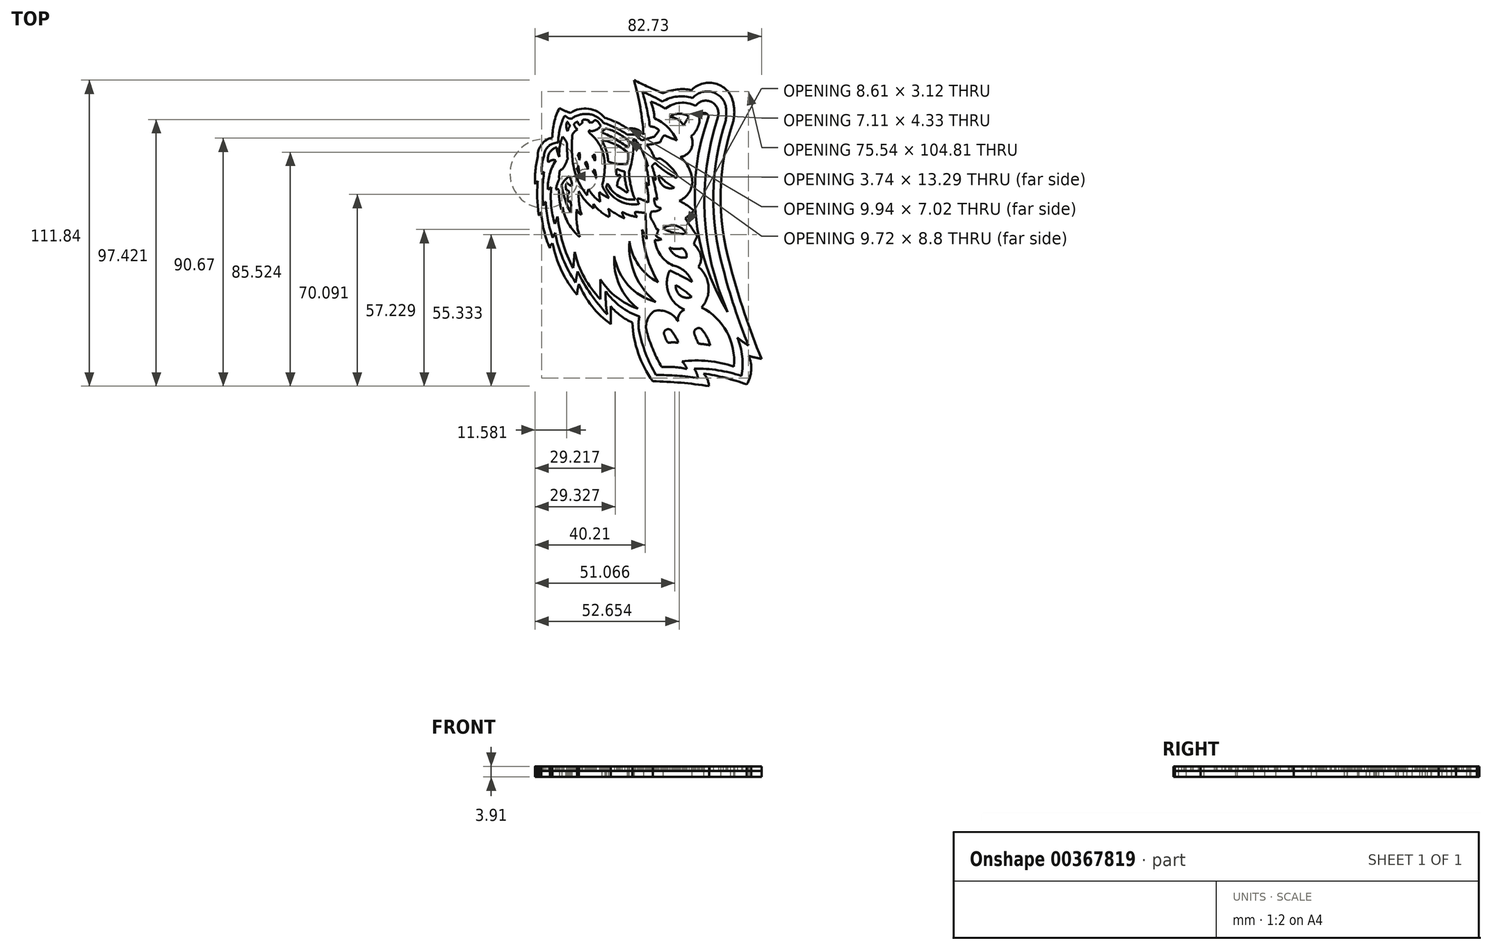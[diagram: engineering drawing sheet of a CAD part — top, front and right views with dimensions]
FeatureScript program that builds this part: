
annotation { "Feature Type Name" : "Feature", "Feature Type Description" : "" }
export const myFeature = defineFeature(function(context is Context, id is Id, definition is map)
    precondition{}
    {
        {
            var Q0;
            Q0=qCreatedBy(makeId("Top.planeOp"),FACE);
            var sketch = newSketch(context, id + "F0", { "sketchPlane" : qUnion([Q0])});
            skLineSegment(sketch, "E0", {"start": v(-9.68, 4.6) * mm, "end": v(-12.98, 4.6) * mm});
            skLineSegment(sketch, "E1", {"start": v(-7.81, 9.13) * mm, "end": v(-5.14, 8.87) * mm});
            skLineSegment(sketch, "E2", {"start": v(-0.46, 12.2) * mm, "end": v(0.77, 11.72) * mm});
            skLineSegment(sketch, "E3", {"start": v(5.28, 13.32) * mm, "end": v(5.62, 12.76) * mm});
            skArc(sketch, "E4", {"start": v(10.1, 12.03) * mm, "mid": v(7.78, 13.04) * mm, "end": v(5.28, 13.32) * mm});
            skArc(sketch, "E5", {"start": v(5.62, 12.76) * mm, "mid": v(2.55, 12.78) * mm, "end": v(-0.46, 12.2) * mm});
            skArc(sketch, "E6", {"start": v(0.77, 11.72) * mm, "mid": v(-3.65, 10.85) * mm, "end": v(-7.81, 9.13) * mm});
            skArc(sketch, "E7", {"start": v(-5.14, 8.87) * mm, "mid": v(-9.36, 7.3) * mm, "end": v(-12.98, 4.6) * mm});
            skArc(sketch, "E8", {"start": v(-9.68, 4.6) * mm, "mid": v(-12.64, 1.92) * mm, "end": v(-14.53, -1.6) * mm});
            skArc(sketch, "E9", {"start": v(-5.85, 2.3) * mm, "mid": v(-10.68, 1.43) * mm, "end": v(-14.53, -1.6) * mm});
            skArc(sketch, "E10", {"start": v(-5.85, 2.3) * mm, "mid": v(-10.66, -0.03) * mm, "end": v(-13.45, -4.58) * mm});
            skArc(sketch, "E11", {"start": v(-3.37, -0.22) * mm, "mid": v(-8.94, -1.17) * mm, "end": v(-13.45, -4.58) * mm});
            skArc(sketch, "E12", {"start": v(-3.37, -0.22) * mm, "mid": v(-7.34, -1.75) * mm, "end": v(-10.14, -4.94) * mm});
            skArc(sketch, "E13", {"start": v(-1.42, -2.32) * mm, "mid": v(-5.93, -3.13) * mm, "end": v(-10.14, -4.94) * mm});
            skArc(sketch, "E14", {"start": v(-1.42, -2.32) * mm, "mid": v(-2.2, -2.67) * mm, "end": v(-2.98, -3.05) * mm});
            skArc(sketch, "E15", {"start": v(-2.98, -3.05) * mm, "mid": v(-0.82, -2.97) * mm, "end": v(1.35, -2.86) * mm});
            skArc(sketch, "E16", {"start": v(1.55, -1.16) * mm, "mid": v(1.44, -2) * mm, "end": v(1.35, -2.86) * mm});
            skArc(sketch, "E17", {"start": v(1.55, -1.16) * mm, "mid": v(1.07, -1.21) * mm, "end": v(0.68, -1.5) * mm});
            skArc(sketch, "E18", {"start": v(1.55, 1.01) * mm, "mid": v(0.98, -0.2) * mm, "end": v(0.68, -1.5) * mm});
            skArc(sketch, "E19", {"start": v(1.55, 1.01) * mm, "mid": v(0.97, 0.86) * mm, "end": v(0.44, 0.6) * mm});
            skArc(sketch, "E20", {"start": v(2.1, 3.35) * mm, "mid": v(1.2, 2.02) * mm, "end": v(0.44, 0.6) * mm});
            skArc(sketch, "E21", {"start": v(0.68, 3.16) * mm, "mid": v(1.4, 3.13) * mm, "end": v(2.1, 3.35) * mm});
            skArc(sketch, "E22", {"start": v(2.8, 5.75) * mm, "mid": v(1.6, 4.58) * mm, "end": v(0.68, 3.16) * mm});
            skArc(sketch, "E23", {"start": v(2.8, 5.75) * mm, "mid": v(2.45, 5.77) * mm, "end": v(2.1, 5.75) * mm});
            skArc(sketch, "E24", {"start": v(4.98, 8.2) * mm, "mid": v(3.41, 7.12) * mm, "end": v(2.1, 5.75) * mm});
            skArc(sketch, "E25", {"start": v(4.98, 8.2) * mm, "mid": v(3, 8.16) * mm, "end": v(1.05, 7.73) * mm});
            skArc(sketch, "E26", {"start": v(1.94, 8.53) * mm, "mid": v(1.4, 8.23) * mm, "end": v(1.05, 7.73) * mm});
            skArc(sketch, "E27", {"start": v(1.94, 8.53) * mm, "mid": v(-0.37, 8.53) * mm, "end": v(-2.64, 8.02) * mm});
            skArc(sketch, "E28", {"start": v(2.29, 10.88) * mm, "mid": v(-0.43, 9.9) * mm, "end": v(-2.64, 8.02) * mm});
            skArc(sketch, "E29", {"start": v(2.29, 10.88) * mm, "mid": v(2.09, 10.98) * mm, "end": v(1.88, 11.07) * mm});
            skArc(sketch, "E30", {"start": v(5.25, 11.51) * mm, "mid": v(3.55, 11.41) * mm, "end": v(1.88, 11.07) * mm});
            skArc(sketch, "E31", {"start": v(5.25, 11.51) * mm, "mid": v(5.3, 11.75) * mm, "end": v(5.25, 11.98) * mm});
            skArc(sketch, "E32", {"start": v(6.95, 11.43) * mm, "mid": v(6.13, 11.8) * mm, "end": v(5.25, 11.98) * mm});
            skArc(sketch, "E33", {"start": v(8.33, 11.35) * mm, "mid": v(7.64, 11.45) * mm, "end": v(6.95, 11.43) * mm});
            skArc(sketch, "E34", {"start": v(8.55, 10.96) * mm, "mid": v(8.5, 11.2) * mm, "end": v(8.33, 11.35) * mm});
            skArc(sketch, "E35", {"start": v(8.55, 10.96) * mm, "mid": v(9.41, 10.45) * mm, "end": v(10.33, 10.05) * mm});
            skArc(sketch, "E36", {"start": v(12.82, 10.15) * mm, "mid": v(11.58, 10.13) * mm, "end": v(10.33, 10.05) * mm});
            skArc(sketch, "E37", {"start": v(12.82, 10.15) * mm, "mid": v(13.46, 10.44) * mm, "end": v(14, 10.88) * mm});
            skArc(sketch, "E38", {"start": v(14, 10.88) * mm, "mid": v(12.37, 11.37) * mm, "end": v(10.67, 11.43) * mm});
            skArc(sketch, "E39", {"start": v(12.27, 11.86) * mm, "mid": v(11.45, 11.74) * mm, "end": v(10.67, 11.43) * mm});
            skArc(sketch, "E40", {"start": v(10.1, 12.03) * mm, "mid": v(10.1, 12.7) * mm, "end": v(9.75, 13.25) * mm});
            skArc(sketch, "E41", {"start": v(12.27, 11.86) * mm, "mid": v(11.3, 13.08) * mm, "end": v(9.75, 13.25) * mm});
            skArc(sketch, "E42", {"start": v(16.51, 10.14) * mm, "mid": v(15.71, 10.28) * mm, "end": v(14.93, 10.05) * mm});
            skArc(sketch, "E43", {"start": v(16.17, 9.93) * mm, "mid": v(16.36, 10) * mm, "end": v(16.51, 10.14) * mm});
            skArc(sketch, "E44", {"start": v(15.52, 9.9) * mm, "mid": v(15.85, 9.7) * mm, "end": v(16.17, 9.93) * mm});
            skArc(sketch, "E45", {"start": v(14.93, 10.05) * mm, "mid": v(15.22, 9.95) * mm, "end": v(15.52, 9.9) * mm});
            skArc(sketch, "E46", {"start": v(6.07, 11.05) * mm, "mid": v(3.67, 10.5) * mm, "end": v(1.42, 9.55) * mm});
            skArc(sketch, "E47", {"start": v(7.46, 9.83) * mm, "mid": v(6.81, 10.5) * mm, "end": v(6.07, 11.05) * mm});
            skArc(sketch, "E48", {"start": v(5.83, 9.35) * mm, "mid": v(6.7, 9.44) * mm, "end": v(7.46, 9.83) * mm});
            skArc(sketch, "E49", {"start": v(6.3, 10.05) * mm, "mid": v(6, 9.74) * mm, "end": v(5.83, 9.35) * mm});
            skArc(sketch, "E50", {"start": v(6.3, 10.05) * mm, "mid": v(6.26, 10.17) * mm, "end": v(6.18, 10.26) * mm});
            skArc(sketch, "E51", {"start": v(6.18, 10.26) * mm, "mid": v(5.66, 10.36) * mm, "end": v(5.14, 10.26) * mm});
            skArc(sketch, "E52", {"start": v(4.58, 9.85) * mm, "mid": v(4.98, 9.89) * mm, "end": v(5.14, 10.26) * mm});
            skArc(sketch, "E53", {"start": v(4.58, 9.85) * mm, "mid": v(4.31, 10.05) * mm, "end": v(3.98, 10.11) * mm});
            skArc(sketch, "E54", {"start": v(3.98, 10.11) * mm, "mid": v(3.54, 10.03) * mm, "end": v(3.14, 9.85) * mm});
            skArc(sketch, "E55", {"start": v(3.35, 9.58) * mm, "mid": v(3.26, 9.72) * mm, "end": v(3.14, 9.85) * mm});
            skArc(sketch, "E56", {"start": v(1.42, 9.55) * mm, "mid": v(2.38, 9.47) * mm, "end": v(3.35, 9.58) * mm});
            skArc(sketch, "E57", {"start": v(10.38, 9.25) * mm, "mid": v(7.14, 8.5) * mm, "end": v(4.28, 6.8) * mm});
            skArc(sketch, "E58", {"start": v(14.46, 9.25) * mm, "mid": v(12.42, 9.35) * mm, "end": v(10.38, 9.25) * mm});
            skArc(sketch, "E59", {"start": v(15.21, 8.4) * mm, "mid": v(14.88, 8.86) * mm, "end": v(14.46, 9.25) * mm});
            skArc(sketch, "E60", {"start": v(16.06, 9.01) * mm, "mid": v(15.59, 8.77) * mm, "end": v(15.21, 8.4) * mm});
            skArc(sketch, "E61", {"start": v(16.54, 8.4) * mm, "mid": v(16.35, 8.74) * mm, "end": v(16.06, 9.01) * mm});
            skArc(sketch, "E62", {"start": v(16.54, 8.4) * mm, "mid": v(16.21, 8.27) * mm, "end": v(15.92, 8.08) * mm});
            skArc(sketch, "E63", {"start": v(16.29, 7.63) * mm, "mid": v(16.12, 7.87) * mm, "end": v(15.92, 8.08) * mm});
            skArc(sketch, "E64", {"start": v(16.8, 7.55) * mm, "mid": v(16.55, 7.62) * mm, "end": v(16.29, 7.63) * mm});
            skArc(sketch, "E65", {"start": v(16.71, 6.51) * mm, "mid": v(16.84, 7.03) * mm, "end": v(16.8, 7.55) * mm});
            skArc(sketch, "E66", {"start": v(16.38, 6.52) * mm, "mid": v(16.55, 6.5) * mm, "end": v(16.71, 6.51) * mm});
            skArc(sketch, "E67", {"start": v(16.38, 6.52) * mm, "mid": v(16.39, 6.2) * mm, "end": v(16.43, 5.9) * mm});
            skArc(sketch, "E68", {"start": v(16.8, 5.4) * mm, "mid": v(16.65, 5.68) * mm, "end": v(16.43, 5.9) * mm});
            skArc(sketch, "E69", {"start": v(15.82, 4.56) * mm, "mid": v(16.37, 4.92) * mm, "end": v(16.8, 5.4) * mm});
            skArc(sketch, "E70", {"start": v(14.95, 6.1) * mm, "mid": v(15.2, 5.23) * mm, "end": v(15.82, 4.56) * mm});
            skArc(sketch, "E71", {"start": v(15.03, 6.33) * mm, "mid": v(14.95, 6.24) * mm, "end": v(14.95, 6.1) * mm});
            skArc(sketch, "E72", {"start": v(15.03, 6.33) * mm, "mid": v(15.02, 6.48) * mm, "end": v(14.88, 6.51) * mm});
            skArc(sketch, "E73", {"start": v(14.88, 6.51) * mm, "mid": v(14.73, 6.48) * mm, "end": v(14.61, 6.38) * mm});
            skArc(sketch, "E74", {"start": v(9.25, 3.89) * mm, "mid": v(12.22, 4.51) * mm, "end": v(14.61, 6.38) * mm});
            skArc(sketch, "E75", {"start": v(5.98, 4.3) * mm, "mid": v(7.6, 3.98) * mm, "end": v(9.25, 3.89) * mm});
            skArc(sketch, "E76", {"start": v(5.98, 4.3) * mm, "mid": v(5.63, 4.2) * mm, "end": v(5.3, 4.04) * mm});
            skArc(sketch, "E77", {"start": v(3.85, 3.19) * mm, "mid": v(4.59, 3.6) * mm, "end": v(5.3, 4.04) * mm});
            skArc(sketch, "E78", {"start": v(4.81, 4.79) * mm, "mid": v(4.27, 4.02) * mm, "end": v(3.85, 3.19) * mm});
            skArc(sketch, "E79", {"start": v(4.81, 4.79) * mm, "mid": v(4, 4.75) * mm, "end": v(3.19, 4.62) * mm});
            skArc(sketch, "E80", {"start": v(5.3, 6.55) * mm, "mid": v(4.13, 5.7) * mm, "end": v(3.19, 4.62) * mm});
            skArc(sketch, "E81", {"start": v(5.3, 6.55) * mm, "mid": v(4.81, 6.76) * mm, "end": v(4.28, 6.8) * mm});
            skArc(sketch, "E82", {"start": v(7.73, 8.16) * mm, "mid": v(8.25, 8.34) * mm, "end": v(8.74, 8.56) * mm});
            skArc(sketch, "E83", {"start": v(8.74, 8.56) * mm, "mid": v(8.94, 8.35) * mm, "end": v(9.23, 8.31) * mm});
            skArc(sketch, "E84", {"start": v(7.73, 8.16) * mm, "mid": v(8.49, 8.18) * mm, "end": v(9.23, 8.31) * mm});
            skArc(sketch, "E85", {"start": v(10.14, 8.12) * mm, "mid": v(10.6, 8.2) * mm, "end": v(11.03, 8.42) * mm});
            skArc(sketch, "E86", {"start": v(11.03, 8.42) * mm, "mid": v(11.18, 8.22) * mm, "end": v(11.42, 8.12) * mm});
            skArc(sketch, "E87", {"start": v(10.14, 8.12) * mm, "mid": v(10.78, 8.02) * mm, "end": v(11.42, 8.12) * mm});
            skArc(sketch, "E88", {"start": v(7.17, 5.33) * mm, "mid": v(7.9, 5.4) * mm, "end": v(8.6, 5.6) * mm});
            skArc(sketch, "E89", {"start": v(8.17, 5.86) * mm, "mid": v(8.38, 5.72) * mm, "end": v(8.6, 5.6) * mm});
            skArc(sketch, "E90", {"start": v(7.17, 5.33) * mm, "mid": v(7.72, 5.51) * mm, "end": v(8.17, 5.86) * mm});
            skArc(sketch, "E91", {"start": v(9.96, 5.53) * mm, "mid": v(10.4, 5.7) * mm, "end": v(10.77, 5.98) * mm});
            skArc(sketch, "E92", {"start": v(10.77, 5.98) * mm, "mid": v(10.9, 5.75) * mm, "end": v(11.15, 5.66) * mm});
            skArc(sketch, "E93", {"start": v(9.96, 5.53) * mm, "mid": v(10.57, 5.48) * mm, "end": v(11.15, 5.66) * mm});
            skArc(sketch, "E94", {"start": v(8.6, 6.68) * mm, "mid": v(9.14, 6.93) * mm, "end": v(9.65, 7.2) * mm});
            skArc(sketch, "E95", {"start": v(9.65, 7.2) * mm, "mid": v(9.74, 7.05) * mm, "end": v(9.88, 6.95) * mm});
            skArc(sketch, "E96", {"start": v(8.6, 6.68) * mm, "mid": v(9.26, 6.73) * mm, "end": v(9.88, 6.95) * mm});
            skArc(sketch, "E97", {"start": v(5.52, 3.63) * mm, "mid": v(3.3, 1.34) * mm, "end": v(2.8, -1.81) * mm});
            skArc(sketch, "E98", {"start": v(3.7, -1.49) * mm, "mid": v(3.25, -1.64) * mm, "end": v(2.8, -1.81) * mm});
            skArc(sketch, "E99", {"start": v(3.64, -2.08) * mm, "mid": v(3.72, -1.79) * mm, "end": v(3.7, -1.49) * mm});
            skArc(sketch, "E100", {"start": v(3.08, -3.32) * mm, "mid": v(3.39, -2.71) * mm, "end": v(3.64, -2.08) * mm});
            skArc(sketch, "E101", {"start": v(3.08, -3.32) * mm, "mid": v(4.74, -3.29) * mm, "end": v(6.35, -2.9) * mm});
            skArc(sketch, "E102", {"start": v(5.9, -3.45) * mm, "mid": v(6.2, -3.23) * mm, "end": v(6.35, -2.9) * mm});
            skArc(sketch, "E103", {"start": v(5.9, -3.45) * mm, "mid": v(7.63, -3.3) * mm, "end": v(9.31, -2.9) * mm});
            skArc(sketch, "E104", {"start": v(9.1, -3.27) * mm, "mid": v(9.24, -3.1) * mm, "end": v(9.31, -2.9) * mm});
            skArc(sketch, "E105", {"start": v(9.1, -3.27) * mm, "mid": v(11.43, -2.43) * mm, "end": v(13.54, -1.16) * mm});
            skArc(sketch, "E106", {"start": v(13.54, -1.16) * mm, "mid": v(13.58, -1) * mm, "end": v(13.54, -0.84) * mm});
            skArc(sketch, "E107", {"start": v(8.15, -0.14) * mm, "mid": v(10.81, -0.75) * mm, "end": v(13.54, -0.84) * mm});
            skArc(sketch, "E108", {"start": v(8.15, -0.14) * mm, "mid": v(5.82, -0.44) * mm, "end": v(3.58, -1.16) * mm});
            skArc(sketch, "E109", {"start": v(6.23, 3.41) * mm, "mid": v(4.15, 1.56) * mm, "end": v(3.58, -1.16) * mm});
            skArc(sketch, "E110", {"start": v(6.23, 3.41) * mm, "mid": v(5.89, 3.57) * mm, "end": v(5.52, 3.63) * mm});
            skArc(sketch, "E111", {"start": v(4.7, 0.16) * mm, "mid": v(5.28, 0.98) * mm, "end": v(5.8, 1.83) * mm});
            skArc(sketch, "E112", {"start": v(4.93, 0) * mm, "mid": v(4.86, 0.15) * mm, "end": v(4.7, 0.16) * mm});
            skArc(sketch, "E113", {"start": v(8.24, 0.59) * mm, "mid": v(6.56, 0.46) * mm, "end": v(4.93, 0) * mm});
            skArc(sketch, "E114", {"start": v(8.6, 1.67) * mm, "mid": v(8.37, 1.15) * mm, "end": v(8.24, 0.59) * mm});
            skArc(sketch, "E115", {"start": v(8.6, 1.67) * mm, "mid": v(8.6, 1.81) * mm, "end": v(8.55, 1.94) * mm});
            skArc(sketch, "E116", {"start": v(8.55, 1.94) * mm, "mid": v(8.1, 1.96) * mm, "end": v(7.66, 1.92) * mm});
            skArc(sketch, "E117", {"start": v(7.66, 1.92) * mm, "mid": v(7.63, 1.7) * mm, "end": v(7.7, 1.47) * mm});
            skArc(sketch, "E118", {"start": v(7.33, 1.33) * mm, "mid": v(7.55, 1.31) * mm, "end": v(7.7, 1.47) * mm});
            skArc(sketch, "E119", {"start": v(7.33, 1.33) * mm, "mid": v(6.6, 1.7) * mm, "end": v(5.8, 1.83) * mm});
            skArc(sketch, "E120", {"start": v(9.88, 3.3) * mm, "mid": v(11.73, 3.65) * mm, "end": v(13.45, 4.39) * mm});
            skArc(sketch, "E121", {"start": v(11.33, 0) * mm, "mid": v(12.7, 2.04) * mm, "end": v(13.45, 4.39) * mm});
            skArc(sketch, "E122", {"start": v(9.52, 0.16) * mm, "mid": v(10.42, -0.02) * mm, "end": v(11.33, 0) * mm});
            skArc(sketch, "E123", {"start": v(9.88, 3.3) * mm, "mid": v(9.5, 1.76) * mm, "end": v(9.52, 0.16) * mm});
            skArc(sketch, "E124", {"start": v(12.2, 0) * mm, "mid": v(13.62, 2.1) * mm, "end": v(14.72, 4.39) * mm});
            skArc(sketch, "E125", {"start": v(15.39, 3.63) * mm, "mid": v(15.11, 4.06) * mm, "end": v(14.72, 4.39) * mm});
            skArc(sketch, "E126", {"start": v(13.45, 0.07) * mm, "mid": v(14.61, 1.75) * mm, "end": v(15.39, 3.63) * mm});
            skArc(sketch, "E127", {"start": v(12.2, 0) * mm, "mid": v(12.83, -0.13) * mm, "end": v(13.45, 0.07) * mm});
            skArc(sketch, "E128", {"start": v(13.02, 11.85) * mm, "mid": v(12.36, 13.32) * mm, "end": v(10.87, 13.95) * mm});
            skArc(sketch, "E129", {"start": v(10.87, 13.95) * mm, "mid": v(9.33, 14.32) * mm, "end": v(7.74, 14.28) * mm});
            skArc(sketch, "E130", {"start": v(8.16, 13.95) * mm, "mid": v(7.98, 14.16) * mm, "end": v(7.74, 14.28) * mm});
            skArc(sketch, "E131", {"start": v(8.16, 13.95) * mm, "mid": v(5.37, 14.2) * mm, "end": v(2.56, 14.1) * mm});
            skArc(sketch, "E132", {"start": v(3.2, 13.67) * mm, "mid": v(2.91, 13.93) * mm, "end": v(2.56, 14.1) * mm});
            skArc(sketch, "E133", {"start": v(3.2, 13.67) * mm, "mid": v(0.16, 13.34) * mm, "end": v(-2.78, 12.53) * mm});
            skArc(sketch, "E134", {"start": v(-1.98, 12.13) * mm, "mid": v(-2.37, 12.36) * mm, "end": v(-2.78, 12.53) * mm});
            skArc(sketch, "E135", {"start": v(-1.98, 12.13) * mm, "mid": v(-6.26, 10.84) * mm, "end": v(-10.2, 8.72) * mm});
            skArc(sketch, "E136", {"start": v(-8.38, 8.4) * mm, "mid": v(-9.3, 8.57) * mm, "end": v(-10.2, 8.72) * mm});
            skArc(sketch, "E137", {"start": v(-8.38, 8.4) * mm, "mid": v(-12.13, 6.22) * mm, "end": v(-15.5, 3.49) * mm});
            skArc(sketch, "E138", {"start": v(-11.68, 3.7) * mm, "mid": v(-13.6, 3.7) * mm, "end": v(-15.5, 3.49) * mm});
            skArc(sketch, "E139", {"start": v(-11.68, 3.7) * mm, "mid": v(-14.21, 1.23) * mm, "end": v(-15.86, -1.9) * mm});
            skArc(sketch, "E140", {"start": v(-24.58, -9.74) * mm, "mid": v(-24.27, -7.67) * mm, "end": v(-24.25, -5.57) * mm});
            skArc(sketch, "E141", {"start": v(-24.58, -9.74) * mm, "mid": v(-23.88, -9.42) * mm, "end": v(-23.3, -8.93) * mm});
            skArc(sketch, "E142", {"start": v(-24.17, -17.55) * mm, "mid": v(-23.26, -13.28) * mm, "end": v(-23.3, -8.93) * mm});
            skArc(sketch, "E143", {"start": v(-24.17, -17.55) * mm, "mid": v(-18.43, -16.4) * mm, "end": v(-14.35, -12.2) * mm});
            skArc(sketch, "E144", {"start": v(-14.35, -12.2) * mm, "mid": v(-10.86, -13.35) * mm, "end": v(-7.61, -11.64) * mm});
            skArc(sketch, "E145", {"start": v(-7.61, -11.64) * mm, "mid": v(-6.2, -12.12) * mm, "end": v(-4.78, -11.64) * mm});
            skArc(sketch, "E146", {"start": v(-4.78, -11.64) * mm, "mid": v(-4.29, -11.32) * mm, "end": v(-3.85, -10.94) * mm});
            skArc(sketch, "E147", {"start": v(-2.55, -11.5) * mm, "mid": v(-3.17, -11.15) * mm, "end": v(-3.85, -10.94) * mm});
            skArc(sketch, "E148", {"start": v(-2.55, -11.5) * mm, "mid": v(-1.05, -10.5) * mm, "end": v(0.45, -9.5) * mm});
            skArc(sketch, "E149", {"start": v(0.45, -9.5) * mm, "mid": v(1.07, -10.24) * mm, "end": v(1.74, -10.94) * mm});
            skArc(sketch, "E150", {"start": v(1.74, -10.94) * mm, "mid": v(2.64, -9.77) * mm, "end": v(3.37, -8.49) * mm});
            skArc(sketch, "E151", {"start": v(3.37, -8.49) * mm, "mid": v(4.6, -10) * mm, "end": v(6.43, -10.67) * mm});
            skArc(sketch, "E152", {"start": v(6.43, -10.67) * mm, "mid": v(8.75, -10.13) * mm, "end": v(10.65, -8.7) * mm});
            skArc(sketch, "E153", {"start": v(10.65, -8.7) * mm, "mid": v(11.92, -10.44) * mm, "end": v(14.08, -10.47) * mm});
            skArc(sketch, "E154", {"start": v(14.08, -10.47) * mm, "mid": v(15.54, -11.55) * mm, "end": v(17.34, -11.86) * mm});
            skArc(sketch, "E155", {"start": v(17.34, -13.36) * mm, "mid": v(17.98, -12.6) * mm, "end": v(17.34, -11.86) * mm});
            skArc(sketch, "E156", {"start": v(17.34, -13.36) * mm, "mid": v(0.74, -11.26) * mm, "end": v(-15.14, -16.54) * mm});
            skArc(sketch, "E157", {"start": v(17.28, -14.9) * mm, "mid": v(0.92, -12.72) * mm, "end": v(-15.14, -16.54) * mm});
            skArc(sketch, "E158", {"start": v(17.28, -14.9) * mm, "mid": v(19.78, -13.86) * mm, "end": v(19.16, -11.23) * mm});
            skArc(sketch, "E159", {"start": v(19.16, -11.23) * mm, "mid": v(19.65, -8.63) * mm, "end": v(18.7, -6.17) * mm});
            skArc(sketch, "E160", {"start": v(17.07, -4.37) * mm, "mid": v(17.1, -4.36) * mm, "end": v(17.13, -4.36) * mm});
            skArc(sketch, "E161", {"start": v(13.39, -8.11) * mm, "mid": v(15.58, -6.59) * mm, "end": v(17.07, -4.37) * mm});
            skArc(sketch, "E162", {"start": v(13.39, -8.11) * mm, "mid": v(13.82, -7.08) * mm, "end": v(14.23, -6.03) * mm});
            skArc(sketch, "E163", {"start": v(14.23, -6.03) * mm, "mid": v(13.74, -5.6) * mm, "end": v(13.13, -5.37) * mm});
            skArc(sketch, "E164", {"start": v(12.66, -3.05) * mm, "mid": v(12.84, -4.22) * mm, "end": v(13.13, -5.37) * mm});
            skArc(sketch, "E165", {"start": v(10.39, -4.36) * mm, "mid": v(11.6, -3.85) * mm, "end": v(12.66, -3.05) * mm});
            skArc(sketch, "E166", {"start": v(10.39, -4.36) * mm, "mid": v(10.36, -4.86) * mm, "end": v(10.39, -5.37) * mm});
            skArc(sketch, "E167", {"start": v(7.66, -8.11) * mm, "mid": v(9.19, -6.9) * mm, "end": v(10.39, -5.37) * mm});
            skArc(sketch, "E168", {"start": v(7.37, -7.66) * mm, "mid": v(7.28, -8.04) * mm, "end": v(7.66, -8.11) * mm});
            skArc(sketch, "E169", {"start": v(9.64, -4.5) * mm, "mid": v(8.39, -6) * mm, "end": v(7.37, -7.66) * mm});
            skArc(sketch, "E170", {"start": v(9.64, -4.5) * mm, "mid": v(9.43, -4.21) * mm, "end": v(9.16, -3.97) * mm});
            skArc(sketch, "E171", {"start": v(6.85, -4.6) * mm, "mid": v(8.01, -4.32) * mm, "end": v(9.16, -3.97) * mm});
            skArc(sketch, "E172", {"start": v(7.37, -4.05) * mm, "mid": v(7.07, -4.3) * mm, "end": v(6.85, -4.6) * mm});
            skArc(sketch, "E173", {"start": v(3.6, -4.84) * mm, "mid": v(5.5, -4.48) * mm, "end": v(7.37, -4.05) * mm});
            skArc(sketch, "E174", {"start": v(3.82, -4.37) * mm, "mid": v(3.66, -4.58) * mm, "end": v(3.6, -4.84) * mm});
            skArc(sketch, "E175", {"start": v(3.82, -4.37) * mm, "mid": v(3.27, -4.36) * mm, "end": v(2.73, -4.5) * mm});
            skArc(sketch, "E176", {"start": v(2.73, -4.5) * mm, "mid": v(2.32, -4.94) * mm, "end": v(2.15, -5.5) * mm});
            skArc(sketch, "E177", {"start": v(1.65, -3.97) * mm, "mid": v(1.68, -4.8) * mm, "end": v(2.15, -5.5) * mm});
            skArc(sketch, "E178", {"start": v(1.65, -3.97) * mm, "mid": v(0.81, -3.7) * mm, "end": v(0, -4.05) * mm});
            skArc(sketch, "E179", {"start": v(-1.39, -4.73) * mm, "mid": v(-0.68, -4.41) * mm, "end": v(0, -4.05) * mm});
            skArc(sketch, "E180", {"start": v(-1.39, -5.02) * mm, "mid": v(-1.36, -4.87) * mm, "end": v(-1.39, -4.73) * mm});
            skArc(sketch, "E181", {"start": v(-2.42, -4.6) * mm, "mid": v(-1.93, -4.87) * mm, "end": v(-1.39, -5.02) * mm});
            skArc(sketch, "E182", {"start": v(-2.42, -4.6) * mm, "mid": v(-2.77, -5.05) * mm, "end": v(-3, -5.56) * mm});
            skArc(sketch, "E183", {"start": v(-3.1, -4.43) * mm, "mid": v(-3.16, -5) * mm, "end": v(-3, -5.56) * mm});
            skArc(sketch, "E184", {"start": v(-3.1, -4.43) * mm, "mid": v(-5.64, -5.37) * mm, "end": v(-7.38, -7.45) * mm});
            skArc(sketch, "E185", {"start": v(-10.1, -10.6) * mm, "mid": v(-8.33, -9.38) * mm, "end": v(-7.38, -7.45) * mm});
            skArc(sketch, "E186", {"start": v(-10.1, -10.6) * mm, "mid": v(-9.1, -8.79) * mm, "end": v(-8.2, -6.91) * mm});
            skArc(sketch, "E187", {"start": v(-8.2, -6.91) * mm, "mid": v(-11.98, -6.74) * mm, "end": v(-14.72, -9.36) * mm});
            skArc(sketch, "E188", {"start": v(-14.72, -9.36) * mm, "mid": v(-15.51, -8.48) * mm, "end": v(-16.68, -8.3) * mm});
            skArc(sketch, "E189", {"start": v(-16.68, -8.3) * mm, "mid": v(-15.15, -6.62) * mm, "end": v(-14.95, -4.36) * mm});
            skArc(sketch, "E190", {"start": v(-14.95, -4.36) * mm, "mid": v(-16.66, -3.1) * mm, "end": v(-18.77, -3.22) * mm});
            skArc(sketch, "E191", {"start": v(-18.77, -3.22) * mm, "mid": v(-21.58, -4.23) * mm, "end": v(-24.25, -5.57) * mm});
            skArc(sketch, "E192", {"start": v(-18.29, -7.24) * mm, "mid": v(-18.03, -6.33) * mm, "end": v(-18.92, -6.02) * mm});
            skArc(sketch, "E193", {"start": v(-18.1, -12.31) * mm, "mid": v(-17.86, -11.37) * mm, "end": v(-18.78, -11.03) * mm});
            skArc(sketch, "E194", {"start": v(-18.78, -11.03) * mm, "mid": v(-19.6, -11.32) * mm, "end": v(-20.38, -11.68) * mm});
            skArc(sketch, "E195", {"start": v(-20.64, -13.62) * mm, "mid": v(-20.48, -12.65) * mm, "end": v(-20.38, -11.68) * mm});
            skArc(sketch, "E196", {"start": v(-20.64, -13.62) * mm, "mid": v(-19.3, -13.1) * mm, "end": v(-18.1, -12.31) * mm});
            skArc(sketch, "E197", {"start": v(-20.22, -8.34) * mm, "mid": v(-19.21, -7.87) * mm, "end": v(-18.29, -7.24) * mm});
            skArc(sketch, "E198", {"start": v(-20.22, -8.34) * mm, "mid": v(-20.16, -7.47) * mm, "end": v(-20.22, -6.61) * mm});
            skArc(sketch, "E199", {"start": v(-18.92, -6.02) * mm, "mid": v(-19.6, -6.27) * mm, "end": v(-20.22, -6.61) * mm});
            skArc(sketch, "E200", {"start": v(-10.64, -7.94) * mm, "mid": v(-12.38, -8.67) * mm, "end": v(-12.6, -10.54) * mm});
            skArc(sketch, "E201", {"start": v(-12.6, -10.54) * mm, "mid": v(-11.54, -9.3) * mm, "end": v(-10.64, -7.94) * mm});
            skArc(sketch, "E202", {"start": v(-4.4, -6.86) * mm, "mid": v(-5.75, -7.98) * mm, "end": v(-6.04, -9.7) * mm});
            skArc(sketch, "E203", {"start": v(-4.4, -6.86) * mm, "mid": v(-4.64, -7.92) * mm, "end": v(-4.52, -9) * mm});
            skArc(sketch, "E204", {"start": v(-6.04, -9.7) * mm, "mid": v(-5.17, -9.59) * mm, "end": v(-4.52, -9) * mm});
            skArc(sketch, "E205", {"start": v(-1.19, -5.8) * mm, "mid": v(-1.97, -7.67) * mm, "end": v(-2.08, -9.7) * mm});
            skArc(sketch, "E206", {"start": v(-2.08, -9.7) * mm, "mid": v(-0.77, -7.95) * mm, "end": v(-1.19, -5.8) * mm});
            skArc(sketch, "E207", {"start": v(7.61, -5.11) * mm, "mid": v(5.87, -5.82) * mm, "end": v(5.56, -7.68) * mm});
            skArc(sketch, "E208", {"start": v(7.61, -5.11) * mm, "mid": v(6.48, -6.3) * mm, "end": v(5.56, -7.68) * mm});
            skArc(sketch, "E209", {"start": v(15.87, -9.22) * mm, "mid": v(16.89, -8.22) * mm, "end": v(17.3, -6.86) * mm});
            skArc(sketch, "E210", {"start": v(17.4, -10.1) * mm, "mid": v(16.65, -9.63) * mm, "end": v(15.87, -9.22) * mm});
            skArc(sketch, "E211", {"start": v(17.4, -10.1) * mm, "mid": v(17.84, -8.46) * mm, "end": v(17.3, -6.86) * mm});
            skArc(sketch, "E212", {"start": v(17.07, -4.37) * mm, "mid": v(18.49, -4.19) * mm, "end": v(19.85, -3.77) * mm});
            skArc(sketch, "E213", {"start": v(18.7, -6.17) * mm, "mid": v(19.35, -5) * mm, "end": v(19.85, -3.77) * mm});
            skArc(sketch, "E214", {"start": v(13.02, 11.85) * mm, "mid": v(13.04, 11.74) * mm, "end": v(13.06, 11.63) * mm});
            skArc(sketch, "E215", {"start": v(17.29, 10.7) * mm, "mid": v(15.22, 11.35) * mm, "end": v(13.06, 11.63) * mm});
            skArc(sketch, "E216", {"start": v(17.33, 10.26) * mm, "mid": v(17.44, 10.49) * mm, "end": v(17.29, 10.7) * mm});
            skArc(sketch, "E217", {"start": v(17.33, 10.26) * mm, "mid": v(17.12, 9.92) * mm, "end": v(17, 9.53) * mm});
            skArc(sketch, "E218", {"start": v(17, 9.53) * mm, "mid": v(17.04, 9.33) * mm, "end": v(17.18, 9.17) * mm});
            skArc(sketch, "E219", {"start": v(17.77, 6.48) * mm, "mid": v(17.7, 7.88) * mm, "end": v(17.18, 9.17) * mm});
            skArc(sketch, "E220", {"start": v(16.33, 4.1) * mm, "mid": v(17.29, 5.15) * mm, "end": v(17.77, 6.48) * mm});
            skArc(sketch, "E221", {"start": v(14.4, 0.14) * mm, "mid": v(15.5, 2.06) * mm, "end": v(16.33, 4.1) * mm});
            skArc(sketch, "E222", {"start": v(14.4, -1.22) * mm, "mid": v(14.4, -0.54) * mm, "end": v(14.4, 0.14) * mm});
            skArc(sketch, "E223", {"start": v(14.4, -1.22) * mm, "mid": v(13.9, -1.76) * mm, "end": v(13.4, -2.31) * mm});
            skArc(sketch, "E224", {"start": v(13.4, -2.31) * mm, "mid": v(13.71, -3.32) * mm, "end": v(14.03, -4.34) * mm});
            skArc(sketch, "E225", {"start": v(14.03, -4.34) * mm, "mid": v(14.47, -4.72) * mm, "end": v(14.93, -5.07) * mm});
            skArc(sketch, "E226", {"start": v(14.93, -5.07) * mm, "mid": v(15.07, -5.1) * mm, "end": v(15.2, -5.07) * mm});
            skArc(sketch, "E227", {"start": v(15.2, -5.07) * mm, "mid": v(15.59, -4.37) * mm, "end": v(15.75, -3.6) * mm});
            skArc(sketch, "E228", {"start": v(15.75, -3.6) * mm, "mid": v(18.66, -3.11) * mm, "end": v(21.51, -2.36) * mm});
            skArc(sketch, "E229", {"start": v(19.87, -5.7) * mm, "mid": v(20.74, -4.05) * mm, "end": v(21.51, -2.36) * mm});
            skArc(sketch, "E230", {"start": v(20.45, -10.71) * mm, "mid": v(20.7, -8.14) * mm, "end": v(19.87, -5.7) * mm});
            skArc(sketch, "E231", {"start": v(19.16, -16.2) * mm, "mid": v(21.47, -13.85) * mm, "end": v(20.45, -10.71) * mm});
            skArc(sketch, "E232", {"start": v(16.74, -16.2) * mm, "mid": v(17.95, -16.3) * mm, "end": v(19.16, -16.2) * mm});
            skArc(sketch, "E233", {"start": v(16.74, -16.2) * mm, "mid": v(4.47, -14.17) * mm, "end": v(-7.86, -15.76) * mm});
            skArc(sketch, "E234", {"start": v(-7.86, -15.76) * mm, "mid": v(-14.34, -17.65) * mm, "end": v(-20.67, -19.99) * mm});
            skArc(sketch, "E235", {"start": v(-19.37, -18.13) * mm, "mid": v(-20.07, -19.03) * mm, "end": v(-20.67, -19.99) * mm});
            skArc(sketch, "E236", {"start": v(-25.73, -18.82) * mm, "mid": v(-22.5, -18.95) * mm, "end": v(-19.37, -18.13) * mm});
            skArc(sketch, "E237", {"start": v(-25.73, -18.82) * mm, "mid": v(-24.8, -14.96) * mm, "end": v(-24.52, -11) * mm});
            skArc(sketch, "E238", {"start": v(-26.1, -11.63) * mm, "mid": v(-25.29, -11.37) * mm, "end": v(-24.52, -11) * mm});
            skArc(sketch, "E239", {"start": v(-26.1, -11.63) * mm, "mid": v(-25.7, -8.14) * mm, "end": v(-25.59, -4.62) * mm});
            skArc(sketch, "E240", {"start": v(-18.2, -1.81) * mm, "mid": v(-22.01, -2.9) * mm, "end": v(-25.59, -4.62) * mm});
            skArc(sketch, "E241", {"start": v(-15.86, -1.9) * mm, "mid": v(-17.03, -1.71) * mm, "end": v(-18.2, -1.81) * mm});
            skArc(sketch, "E242", {"start": v(-14.16, 2.89) * mm, "mid": v(-15.64, 2.9) * mm, "end": v(-17.12, 2.87) * mm});
            skArc(sketch, "E243", {"start": v(-14.16, 2.89) * mm, "mid": v(-15.72, 1.25) * mm, "end": v(-16.86, -0.7) * mm});
            skArc(sketch, "E244", {"start": v(-16.86, -0.7) * mm, "mid": v(-21.99, -1.68) * mm, "end": v(-26.62, -4.1) * mm});
            skArc(sketch, "E245", {"start": v(-27.42, -13.43) * mm, "mid": v(-26.86, -8.78) * mm, "end": v(-26.62, -4.1) * mm});
            skArc(sketch, "E246", {"start": v(-27.42, -13.43) * mm, "mid": v(-26.3, -13.17) * mm, "end": v(-25.33, -12.54) * mm});
            skArc(sketch, "E247", {"start": v(-27.15, -19.7) * mm, "mid": v(-26.06, -16.17) * mm, "end": v(-25.33, -12.54) * mm});
            skArc(sketch, "E248", {"start": v(-27.15, -19.7) * mm, "mid": v(-24.8, -20.43) * mm, "end": v(-22.39, -20.03) * mm});
            skArc(sketch, "E249", {"start": v(-22.39, -20.03) * mm, "mid": v(-22.68, -21.08) * mm, "end": v(-22.9, -22.15) * mm});
            skArc(sketch, "E250", {"start": v(-7.43, -16.97) * mm, "mid": v(-15.25, -19.3) * mm, "end": v(-22.9, -22.15) * mm});
            skArc(sketch, "E251", {"start": v(16.66, -17.48) * mm, "mid": v(4.66, -15.37) * mm, "end": v(-7.43, -16.97) * mm});
            skArc(sketch, "E252", {"start": v(16.66, -17.48) * mm, "mid": v(18.1, -17.64) * mm, "end": v(19.54, -17.48) * mm});
            skArc(sketch, "E253", {"start": v(19.54, -17.48) * mm, "mid": v(22.8, -14.7) * mm, "end": v(21.78, -10.54) * mm});
            skArc(sketch, "E254", {"start": v(21.78, -10.54) * mm, "mid": v(21.87, -8.13) * mm, "end": v(21.25, -5.8) * mm});
            skArc(sketch, "E255", {"start": v(23.41, -0.97) * mm, "mid": v(22.29, -3.37) * mm, "end": v(21.25, -5.8) * mm});
            skArc(sketch, "E256", {"start": v(14.39, -2.56) * mm, "mid": v(18.94, -2) * mm, "end": v(23.41, -0.97) * mm});
            skArc(sketch, "E257", {"start": v(14.39, -2.56) * mm, "mid": v(15.26, -1.42) * mm, "end": v(15.33, 0) * mm});
            skArc(sketch, "E258", {"start": v(15.33, 0) * mm, "mid": v(16.38, 1.86) * mm, "end": v(17.15, 3.85) * mm});
            skArc(sketch, "E259", {"start": v(17.15, 3.85) * mm, "mid": v(18.66, 6.56) * mm, "end": v(17.98, 9.6) * mm});
            skArc(sketch, "E260", {"start": v(18.75, 11.41) * mm, "mid": v(18.32, 10.52) * mm, "end": v(17.98, 9.6) * mm});
            skArc(sketch, "E261", {"start": v(18.75, 11.41) * mm, "mid": v(16.4, 12.3) * mm, "end": v(13.9, 12.55) * mm});
            skArc(sketch, "E262", {"start": v(13.9, 12.55) * mm, "mid": v(12.76, 14.35) * mm, "end": v(10.74, 15.02) * mm});
            skArc(sketch, "E263", {"start": v(10.74, 15.02) * mm, "mid": v(8.46, 15.4) * mm, "end": v(6.14, 15.43) * mm});
            skArc(sketch, "E264", {"start": v(6.63, 15.02) * mm, "mid": v(6.43, 15.28) * mm, "end": v(6.14, 15.43) * mm});
            skArc(sketch, "E265", {"start": v(6.63, 15.02) * mm, "mid": v(3.78, 15.1) * mm, "end": v(0.94, 14.81) * mm});
            skArc(sketch, "E266", {"start": v(1.45, 14.45) * mm, "mid": v(1.22, 14.68) * mm, "end": v(0.94, 14.81) * mm});
            skArc(sketch, "E267", {"start": v(1.45, 14.45) * mm, "mid": v(-1.6, 13.97) * mm, "end": v(-4.52, 13) * mm});
            skArc(sketch, "E268", {"start": v(-3.7, 12.55) * mm, "mid": v(-4.05, 12.89) * mm, "end": v(-4.52, 13) * mm});
            skArc(sketch, "E269", {"start": v(-3.7, 12.55) * mm, "mid": v(-8.24, 11.07) * mm, "end": v(-12.25, 8.5) * mm});
            skArc(sketch, "E270", {"start": v(-10.42, 8.18) * mm, "mid": v(-11.33, 8.37) * mm, "end": v(-12.25, 8.5) * mm});
            skArc(sketch, "E271", {"start": v(-10.42, 8.18) * mm, "mid": v(-14.16, 6.02) * mm, "end": v(-17.12, 2.87) * mm});
            skLineSegment(sketch, "E272", {"start": v(-4.94, 16.73) * mm, "end": v(-17.06, 19.36) * mm});
            skSolve(sketch);
        }
        {
            var Q0;
            Q0=makeQuery(id+"F0.imprint","IMPRINT",FACE,{"disambiguationData":[TD([[makeQuery(id+"F0.imprint","IMPRINT",EDGE,{"derivedFrom":sQuery(id+"F0.wireOp",EDGE,"E128")}),-1.0]])]});
            var Q1;
            Q1=makeQuery(id+"F0.imprint","IMPRINT",FACE,{"disambiguationData":[TD([[makeQuery(id+"F0.imprint","IMPRINT",EDGE,{"derivedFrom":sQuery(id+"F0.wireOp",EDGE,"E193")}),1.0]])]});
            var Q2;
            Q2=makeQuery(id+"F0.imprint","IMPRINT",FACE,{"disambiguationData":[TD([[makeQuery(id+"F0.imprint","IMPRINT",EDGE,{"derivedFrom":sQuery(id+"F0.wireOp",EDGE,"E192")}),1.0]])]});
            var Q3;
            Q3=makeQuery(id+"F0.imprint","IMPRINT",FACE,{"disambiguationData":[TD([[makeQuery(id+"F0.imprint","IMPRINT",EDGE,{"derivedFrom":sQuery(id+"F0.wireOp",EDGE,"E200")}),1.0]])]});
            var Q4;
            Q4=makeQuery(id+"F0.imprint","IMPRINT",FACE,{"disambiguationData":[TD([[makeQuery(id+"F0.imprint","IMPRINT",EDGE,{"derivedFrom":sQuery(id+"F0.wireOp",EDGE,"E202")}),1.0]])]});
            var Q5;
            Q5=makeQuery(id+"F0.imprint","IMPRINT",FACE,{"disambiguationData":[TD([[makeQuery(id+"F0.imprint","IMPRINT",EDGE,{"derivedFrom":sQuery(id+"F0.wireOp",EDGE,"E205")}),1.0]])]});
            var Q6;
            Q6=makeQuery(id+"F0.imprint","IMPRINT",FACE,{"disambiguationData":[TD([[makeQuery(id+"F0.imprint","IMPRINT",EDGE,{"derivedFrom":sQuery(id+"F0.wireOp",EDGE,"E209")}),-1.0]])]});
            var Q7;
            Q7=makeQuery(id+"F0.imprint","IMPRINT",FACE,{"disambiguationData":[TD([[makeQuery(id+"F0.imprint","IMPRINT",EDGE,{"derivedFrom":sQuery(id+"F0.wireOp",EDGE,"E111")}),-1.0]])]});
            var Q8;
            Q8=makeQuery(id+"F0.imprint","IMPRINT",FACE,{"disambiguationData":[TD([[makeQuery(id+"F0.imprint","IMPRINT",EDGE,{"derivedFrom":sQuery(id+"F0.wireOp",EDGE,"E0")}),1.0]])]});
            var Q9;
            Q9=makeQuery(id+"F0.imprint","IMPRINT",FACE,{"disambiguationData":[TD([[makeQuery(id+"F0.imprint","IMPRINT",EDGE,{"derivedFrom":sQuery(id+"F0.wireOp",EDGE,"E94")}),-1.0]])]});
            var Q10;
            Q10=makeQuery(id+"F0.imprint","IMPRINT",FACE,{"disambiguationData":[TD([[makeQuery(id+"F0.imprint","IMPRINT",EDGE,{"derivedFrom":sQuery(id+"F0.wireOp",EDGE,"E85")}),-1.0]])]});
            var Q11;
            Q11=makeQuery(id+"F0.imprint","IMPRINT",FACE,{"disambiguationData":[TD([[makeQuery(id+"F0.imprint","IMPRINT",EDGE,{"derivedFrom":sQuery(id+"F0.wireOp",EDGE,"E42")}),1.0]])]});
            var Q12;
            Q12=makeQuery(id+"F0.imprint","IMPRINT",FACE,{"disambiguationData":[TD([[makeQuery(id+"F0.imprint","IMPRINT",EDGE,{"derivedFrom":sQuery(id+"F0.wireOp",EDGE,"E0")}),-1.0]])]});
            var Q13;
            Q13=makeQuery(id+"F0.imprint","IMPRINT",FACE,{"disambiguationData":[TD([[makeQuery(id+"F0.imprint","IMPRINT",EDGE,{"derivedFrom":sQuery(id+"F0.wireOp",EDGE,"E140")}),-1.0]])]});
            var Q14;
            Q14=makeQuery(id+"F0.imprint","IMPRINT",FACE,{"disambiguationData":[TD([[makeQuery(id+"F0.imprint","IMPRINT",EDGE,{"derivedFrom":sQuery(id+"F0.wireOp",EDGE,"E97")}),1.0]])]});
            var Q15;
            Q15=makeQuery(id+"F0.imprint","IMPRINT",FACE,{"disambiguationData":[TD([[makeQuery(id+"F0.imprint","IMPRINT",EDGE,{"derivedFrom":sQuery(id+"F0.wireOp",EDGE,"E57")}),1.0]])]});
            var Q16;
            Q16=makeQuery(id+"F0.imprint","IMPRINT",FACE,{"disambiguationData":[TD([[makeQuery(id+"F0.imprint","IMPRINT",EDGE,{"derivedFrom":sQuery(id+"F0.wireOp",EDGE,"E207")}),1.0]])]});
            var Q17;
            Q17=makeQuery(id+"F0.imprint","IMPRINT",FACE,{"disambiguationData":[TD([[makeQuery(id+"F0.imprint","IMPRINT",EDGE,{"derivedFrom":sQuery(id+"F0.wireOp",EDGE,"E91")}),-1.0]])]});
            var Q18;
            Q18=makeQuery(id+"F0.imprint","IMPRINT",FACE,{"disambiguationData":[TD([[makeQuery(id+"F0.imprint","IMPRINT",EDGE,{"derivedFrom":sQuery(id+"F0.wireOp",EDGE,"E88")}),1.0]])]});
            var Q19;
            Q19=makeQuery(id+"F0.imprint","IMPRINT",FACE,{"disambiguationData":[TD([[makeQuery(id+"F0.imprint","IMPRINT",EDGE,{"derivedFrom":sQuery(id+"F0.wireOp",EDGE,"E82")}),-1.0]])]});
            extrude(context, id + "F1", {"entities" : qUnion([Q0, Q1, Q2, Q3, Q4, Q5, Q6, Q7, Q8, Q9, Q10, Q11, Q12, Q13, Q14, Q15, Q16, Q17, Q18, Q19]), "depth" : 1.02 * mm});
        }
        {
            var Q0;
            Q0=makeQuery(id+"F0.imprint","IMPRINT",FACE,{"disambiguationData":[TD([[makeQuery(id+"F0.imprint","IMPRINT",EDGE,{"derivedFrom":sQuery(id+"F0.wireOp",EDGE,"E0")}),1.0]])]});
            var Q1;
            Q1=makeQuery(id+"F0.imprint","IMPRINT",FACE,{"disambiguationData":[TD([[makeQuery(id+"F0.imprint","IMPRINT",EDGE,{"derivedFrom":sQuery(id+"F0.wireOp",EDGE,"E94")}),-1.0]])]});
            var Q2;
            Q2=makeQuery(id+"F0.imprint","IMPRINT",FACE,{"disambiguationData":[TD([[makeQuery(id+"F0.imprint","IMPRINT",EDGE,{"derivedFrom":sQuery(id+"F0.wireOp",EDGE,"E82")}),-1.0]])]});
            var Q3;
            Q3=makeQuery(id+"F0.imprint","IMPRINT",FACE,{"disambiguationData":[TD([[makeQuery(id+"F0.imprint","IMPRINT",EDGE,{"derivedFrom":sQuery(id+"F0.wireOp",EDGE,"E85")}),-1.0]])]});
            var Q4;
            Q4=makeQuery(id+"F0.imprint","IMPRINT",FACE,{"disambiguationData":[TD([[makeQuery(id+"F0.imprint","IMPRINT",EDGE,{"derivedFrom":sQuery(id+"F0.wireOp",EDGE,"E91")}),-1.0]])]});
            var Q5;
            Q5=makeQuery(id+"F0.imprint","IMPRINT",FACE,{"disambiguationData":[TD([[makeQuery(id+"F0.imprint","IMPRINT",EDGE,{"derivedFrom":sQuery(id+"F0.wireOp",EDGE,"E88")}),1.0]])]});
            var Q6;
            Q6=makeQuery(id+"F0.imprint","IMPRINT",FACE,{"disambiguationData":[TD([[makeQuery(id+"F0.imprint","IMPRINT",EDGE,{"derivedFrom":sQuery(id+"F0.wireOp",EDGE,"E209")}),-1.0]])]});
            var Q7;
            Q7=makeQuery(id+"F0.imprint","IMPRINT",FACE,{"disambiguationData":[TD([[makeQuery(id+"F0.imprint","IMPRINT",EDGE,{"derivedFrom":sQuery(id+"F0.wireOp",EDGE,"E207")}),1.0]])]});
            var Q8;
            Q8=makeQuery(id+"F0.imprint","IMPRINT",FACE,{"disambiguationData":[TD([[makeQuery(id+"F0.imprint","IMPRINT",EDGE,{"derivedFrom":sQuery(id+"F0.wireOp",EDGE,"E205")}),1.0]])]});
            var Q9;
            Q9=makeQuery(id+"F0.imprint","IMPRINT",FACE,{"disambiguationData":[TD([[makeQuery(id+"F0.imprint","IMPRINT",EDGE,{"derivedFrom":sQuery(id+"F0.wireOp",EDGE,"E202")}),1.0]])]});
            var Q10;
            Q10=makeQuery(id+"F0.imprint","IMPRINT",FACE,{"disambiguationData":[TD([[makeQuery(id+"F0.imprint","IMPRINT",EDGE,{"derivedFrom":sQuery(id+"F0.wireOp",EDGE,"E200")}),1.0]])]});
            var Q11;
            Q11=makeQuery(id+"F0.imprint","IMPRINT",FACE,{"disambiguationData":[TD([[makeQuery(id+"F0.imprint","IMPRINT",EDGE,{"derivedFrom":sQuery(id+"F0.wireOp",EDGE,"E193")}),1.0]])]});
            var Q12;
            Q12=makeQuery(id+"F0.imprint","IMPRINT",FACE,{"disambiguationData":[TD([[makeQuery(id+"F0.imprint","IMPRINT",EDGE,{"derivedFrom":sQuery(id+"F0.wireOp",EDGE,"E192")}),1.0]])]});
            extrude(context, id + "F2", {"entities" : qUnion([Q0, Q1, Q2, Q3, Q4, Q5, Q6, Q7, Q8, Q9, Q10, Q11, Q12]), "operationType" : NewBodyOperationType.ADD, "depth" : 1.04 * mm});
        }
        {
            var Q0;
            Q0=makeQuery(id+"F2.boolean.opBoolean","SPLIT",FACE,{"disambiguationData":[TD([makeQuery(id+"F2.opExtrude","SWEPT_FACE",FACE,{"disambiguationData":[OSD([sQuery(id+"F0.wireOp",EDGE,"E0")])]})])],"derivedFrom":makeQuery(id+"F1.opExtrude","CAP_FACE",FACE,{"disambiguationData":[OSD([sQuery(id+"F0.wireOp",EDGE,"E46"),sQuery(id+"F0.wireOp",EDGE,"E47"),sQuery(id+"F0.wireOp",EDGE,"E48"),sQuery(id+"F0.wireOp",EDGE,"E49"),sQuery(id+"F0.wireOp",EDGE,"E50"),sQuery(id+"F0.wireOp",EDGE,"E51"),sQuery(id+"F0.wireOp",EDGE,"E52"),sQuery(id+"F0.wireOp",EDGE,"E53"),sQuery(id+"F0.wireOp",EDGE,"E54"),sQuery(id+"F0.wireOp",EDGE,"E55"),sQuery(id+"F0.wireOp",EDGE,"E56"),sQuery(id+"F0.wireOp",EDGE,"E120"),sQuery(id+"F0.wireOp",EDGE,"E121"),sQuery(id+"F0.wireOp",EDGE,"E122"),sQuery(id+"F0.wireOp",EDGE,"E123"),sQuery(id+"F0.wireOp",EDGE,"E124"),sQuery(id+"F0.wireOp",EDGE,"E125"),sQuery(id+"F0.wireOp",EDGE,"E126"),sQuery(id+"F0.wireOp",EDGE,"E127"),sQuery(id+"F0.wireOp",EDGE,"E242"),sQuery(id+"F0.wireOp",EDGE,"E243"),sQuery(id+"F0.wireOp",EDGE,"E244"),sQuery(id+"F0.wireOp",EDGE,"E245"),sQuery(id+"F0.wireOp",EDGE,"E246"),sQuery(id+"F0.wireOp",EDGE,"E247"),sQuery(id+"F0.wireOp",EDGE,"E248"),sQuery(id+"F0.wireOp",EDGE,"E249"),sQuery(id+"F0.wireOp",EDGE,"E250"),sQuery(id+"F0.wireOp",EDGE,"E251"),sQuery(id+"F0.wireOp",EDGE,"E252"),sQuery(id+"F0.wireOp",EDGE,"E253"),sQuery(id+"F0.wireOp",EDGE,"E254"),sQuery(id+"F0.wireOp",EDGE,"E255"),sQuery(id+"F0.wireOp",EDGE,"E256"),sQuery(id+"F0.wireOp",EDGE,"E257"),sQuery(id+"F0.wireOp",EDGE,"E258"),sQuery(id+"F0.wireOp",EDGE,"E259"),sQuery(id+"F0.wireOp",EDGE,"E260"),sQuery(id+"F0.wireOp",EDGE,"E261"),sQuery(id+"F0.wireOp",EDGE,"E262"),sQuery(id+"F0.wireOp",EDGE,"E263"),sQuery(id+"F0.wireOp",EDGE,"E264"),sQuery(id+"F0.wireOp",EDGE,"E265"),sQuery(id+"F0.wireOp",EDGE,"E266"),sQuery(id+"F0.wireOp",EDGE,"E267"),sQuery(id+"F0.wireOp",EDGE,"E268"),sQuery(id+"F0.wireOp",EDGE,"E269"),sQuery(id+"F0.wireOp",EDGE,"E270"),sQuery(id+"F0.wireOp",EDGE,"E271")])],"isStart":false})});
            var Q1;
            Q1=makeQuery(id+"F2.boolean.opBoolean","SPLIT",FACE,{"disambiguationData":[TD([makeQuery(id+"F2.opExtrude","SWEPT_FACE",FACE,{"disambiguationData":[OSD([sQuery(id+"F0.wireOp",EDGE,"E57")])]})])],"derivedFrom":makeQuery(id+"F1.opExtrude","CAP_FACE",FACE,{"disambiguationData":[OSD([sQuery(id+"F0.wireOp",EDGE,"E46"),sQuery(id+"F0.wireOp",EDGE,"E47"),sQuery(id+"F0.wireOp",EDGE,"E48"),sQuery(id+"F0.wireOp",EDGE,"E49"),sQuery(id+"F0.wireOp",EDGE,"E50"),sQuery(id+"F0.wireOp",EDGE,"E51"),sQuery(id+"F0.wireOp",EDGE,"E52"),sQuery(id+"F0.wireOp",EDGE,"E53"),sQuery(id+"F0.wireOp",EDGE,"E54"),sQuery(id+"F0.wireOp",EDGE,"E55"),sQuery(id+"F0.wireOp",EDGE,"E56"),sQuery(id+"F0.wireOp",EDGE,"E120"),sQuery(id+"F0.wireOp",EDGE,"E121"),sQuery(id+"F0.wireOp",EDGE,"E122"),sQuery(id+"F0.wireOp",EDGE,"E123"),sQuery(id+"F0.wireOp",EDGE,"E124"),sQuery(id+"F0.wireOp",EDGE,"E125"),sQuery(id+"F0.wireOp",EDGE,"E126"),sQuery(id+"F0.wireOp",EDGE,"E127"),sQuery(id+"F0.wireOp",EDGE,"E242"),sQuery(id+"F0.wireOp",EDGE,"E243"),sQuery(id+"F0.wireOp",EDGE,"E244"),sQuery(id+"F0.wireOp",EDGE,"E245"),sQuery(id+"F0.wireOp",EDGE,"E246"),sQuery(id+"F0.wireOp",EDGE,"E247"),sQuery(id+"F0.wireOp",EDGE,"E248"),sQuery(id+"F0.wireOp",EDGE,"E249"),sQuery(id+"F0.wireOp",EDGE,"E250"),sQuery(id+"F0.wireOp",EDGE,"E251"),sQuery(id+"F0.wireOp",EDGE,"E252"),sQuery(id+"F0.wireOp",EDGE,"E253"),sQuery(id+"F0.wireOp",EDGE,"E254"),sQuery(id+"F0.wireOp",EDGE,"E255"),sQuery(id+"F0.wireOp",EDGE,"E256"),sQuery(id+"F0.wireOp",EDGE,"E257"),sQuery(id+"F0.wireOp",EDGE,"E258"),sQuery(id+"F0.wireOp",EDGE,"E259"),sQuery(id+"F0.wireOp",EDGE,"E260"),sQuery(id+"F0.wireOp",EDGE,"E261"),sQuery(id+"F0.wireOp",EDGE,"E262"),sQuery(id+"F0.wireOp",EDGE,"E263"),sQuery(id+"F0.wireOp",EDGE,"E264"),sQuery(id+"F0.wireOp",EDGE,"E265"),sQuery(id+"F0.wireOp",EDGE,"E266"),sQuery(id+"F0.wireOp",EDGE,"E267"),sQuery(id+"F0.wireOp",EDGE,"E268"),sQuery(id+"F0.wireOp",EDGE,"E269"),sQuery(id+"F0.wireOp",EDGE,"E270"),sQuery(id+"F0.wireOp",EDGE,"E271")])],"isStart":false})});
            var Q2;
            Q2=makeQuery(id+"F2.boolean.opBoolean","SPLIT",FACE,{"disambiguationData":[TD([makeQuery(id+"F2.opExtrude","SWEPT_FACE",FACE,{"disambiguationData":[OSD([sQuery(id+"F0.wireOp",EDGE,"E97")])]})])],"derivedFrom":makeQuery(id+"F1.opExtrude","CAP_FACE",FACE,{"disambiguationData":[OSD([sQuery(id+"F0.wireOp",EDGE,"E46"),sQuery(id+"F0.wireOp",EDGE,"E47"),sQuery(id+"F0.wireOp",EDGE,"E48"),sQuery(id+"F0.wireOp",EDGE,"E49"),sQuery(id+"F0.wireOp",EDGE,"E50"),sQuery(id+"F0.wireOp",EDGE,"E51"),sQuery(id+"F0.wireOp",EDGE,"E52"),sQuery(id+"F0.wireOp",EDGE,"E53"),sQuery(id+"F0.wireOp",EDGE,"E54"),sQuery(id+"F0.wireOp",EDGE,"E55"),sQuery(id+"F0.wireOp",EDGE,"E56"),sQuery(id+"F0.wireOp",EDGE,"E120"),sQuery(id+"F0.wireOp",EDGE,"E121"),sQuery(id+"F0.wireOp",EDGE,"E122"),sQuery(id+"F0.wireOp",EDGE,"E123"),sQuery(id+"F0.wireOp",EDGE,"E124"),sQuery(id+"F0.wireOp",EDGE,"E125"),sQuery(id+"F0.wireOp",EDGE,"E126"),sQuery(id+"F0.wireOp",EDGE,"E127"),sQuery(id+"F0.wireOp",EDGE,"E242"),sQuery(id+"F0.wireOp",EDGE,"E243"),sQuery(id+"F0.wireOp",EDGE,"E244"),sQuery(id+"F0.wireOp",EDGE,"E245"),sQuery(id+"F0.wireOp",EDGE,"E246"),sQuery(id+"F0.wireOp",EDGE,"E247"),sQuery(id+"F0.wireOp",EDGE,"E248"),sQuery(id+"F0.wireOp",EDGE,"E249"),sQuery(id+"F0.wireOp",EDGE,"E250"),sQuery(id+"F0.wireOp",EDGE,"E251"),sQuery(id+"F0.wireOp",EDGE,"E252"),sQuery(id+"F0.wireOp",EDGE,"E253"),sQuery(id+"F0.wireOp",EDGE,"E254"),sQuery(id+"F0.wireOp",EDGE,"E255"),sQuery(id+"F0.wireOp",EDGE,"E256"),sQuery(id+"F0.wireOp",EDGE,"E257"),sQuery(id+"F0.wireOp",EDGE,"E258"),sQuery(id+"F0.wireOp",EDGE,"E259"),sQuery(id+"F0.wireOp",EDGE,"E260"),sQuery(id+"F0.wireOp",EDGE,"E261"),sQuery(id+"F0.wireOp",EDGE,"E262"),sQuery(id+"F0.wireOp",EDGE,"E263"),sQuery(id+"F0.wireOp",EDGE,"E264"),sQuery(id+"F0.wireOp",EDGE,"E265"),sQuery(id+"F0.wireOp",EDGE,"E266"),sQuery(id+"F0.wireOp",EDGE,"E267"),sQuery(id+"F0.wireOp",EDGE,"E268"),sQuery(id+"F0.wireOp",EDGE,"E269"),sQuery(id+"F0.wireOp",EDGE,"E270"),sQuery(id+"F0.wireOp",EDGE,"E271")])],"isStart":false})});
            var Q3;
            Q3=makeQuery(id+"F2.boolean.opBoolean","SPLIT",FACE,{"disambiguationData":[TD([makeQuery(id+"F2.opExtrude","SWEPT_FACE",FACE,{"disambiguationData":[OSD([sQuery(id+"F0.wireOp",EDGE,"E42")])]})])],"derivedFrom":makeQuery(id+"F1.opExtrude","CAP_FACE",FACE,{"disambiguationData":[OSD([sQuery(id+"F0.wireOp",EDGE,"E46"),sQuery(id+"F0.wireOp",EDGE,"E47"),sQuery(id+"F0.wireOp",EDGE,"E48"),sQuery(id+"F0.wireOp",EDGE,"E49"),sQuery(id+"F0.wireOp",EDGE,"E50"),sQuery(id+"F0.wireOp",EDGE,"E51"),sQuery(id+"F0.wireOp",EDGE,"E52"),sQuery(id+"F0.wireOp",EDGE,"E53"),sQuery(id+"F0.wireOp",EDGE,"E54"),sQuery(id+"F0.wireOp",EDGE,"E55"),sQuery(id+"F0.wireOp",EDGE,"E56"),sQuery(id+"F0.wireOp",EDGE,"E120"),sQuery(id+"F0.wireOp",EDGE,"E121"),sQuery(id+"F0.wireOp",EDGE,"E122"),sQuery(id+"F0.wireOp",EDGE,"E123"),sQuery(id+"F0.wireOp",EDGE,"E124"),sQuery(id+"F0.wireOp",EDGE,"E125"),sQuery(id+"F0.wireOp",EDGE,"E126"),sQuery(id+"F0.wireOp",EDGE,"E127"),sQuery(id+"F0.wireOp",EDGE,"E242"),sQuery(id+"F0.wireOp",EDGE,"E243"),sQuery(id+"F0.wireOp",EDGE,"E244"),sQuery(id+"F0.wireOp",EDGE,"E245"),sQuery(id+"F0.wireOp",EDGE,"E246"),sQuery(id+"F0.wireOp",EDGE,"E247"),sQuery(id+"F0.wireOp",EDGE,"E248"),sQuery(id+"F0.wireOp",EDGE,"E249"),sQuery(id+"F0.wireOp",EDGE,"E250"),sQuery(id+"F0.wireOp",EDGE,"E251"),sQuery(id+"F0.wireOp",EDGE,"E252"),sQuery(id+"F0.wireOp",EDGE,"E253"),sQuery(id+"F0.wireOp",EDGE,"E254"),sQuery(id+"F0.wireOp",EDGE,"E255"),sQuery(id+"F0.wireOp",EDGE,"E256"),sQuery(id+"F0.wireOp",EDGE,"E257"),sQuery(id+"F0.wireOp",EDGE,"E258"),sQuery(id+"F0.wireOp",EDGE,"E259"),sQuery(id+"F0.wireOp",EDGE,"E260"),sQuery(id+"F0.wireOp",EDGE,"E261"),sQuery(id+"F0.wireOp",EDGE,"E262"),sQuery(id+"F0.wireOp",EDGE,"E263"),sQuery(id+"F0.wireOp",EDGE,"E264"),sQuery(id+"F0.wireOp",EDGE,"E265"),sQuery(id+"F0.wireOp",EDGE,"E266"),sQuery(id+"F0.wireOp",EDGE,"E267"),sQuery(id+"F0.wireOp",EDGE,"E268"),sQuery(id+"F0.wireOp",EDGE,"E269"),sQuery(id+"F0.wireOp",EDGE,"E270"),sQuery(id+"F0.wireOp",EDGE,"E271")])],"isStart":false})});
            var Q4;
            Q4=makeQuery(id+"F2.boolean.opBoolean","SPLIT",FACE,{"disambiguationData":[TD([makeQuery(id+"F2.opExtrude","SWEPT_FACE",FACE,{"disambiguationData":[OSD([sQuery(id+"F0.wireOp",EDGE,"E111")])]})])],"derivedFrom":makeQuery(id+"F1.opExtrude","CAP_FACE",FACE,{"disambiguationData":[OSD([sQuery(id+"F0.wireOp",EDGE,"E46"),sQuery(id+"F0.wireOp",EDGE,"E47"),sQuery(id+"F0.wireOp",EDGE,"E48"),sQuery(id+"F0.wireOp",EDGE,"E49"),sQuery(id+"F0.wireOp",EDGE,"E50"),sQuery(id+"F0.wireOp",EDGE,"E51"),sQuery(id+"F0.wireOp",EDGE,"E52"),sQuery(id+"F0.wireOp",EDGE,"E53"),sQuery(id+"F0.wireOp",EDGE,"E54"),sQuery(id+"F0.wireOp",EDGE,"E55"),sQuery(id+"F0.wireOp",EDGE,"E56"),sQuery(id+"F0.wireOp",EDGE,"E120"),sQuery(id+"F0.wireOp",EDGE,"E121"),sQuery(id+"F0.wireOp",EDGE,"E122"),sQuery(id+"F0.wireOp",EDGE,"E123"),sQuery(id+"F0.wireOp",EDGE,"E124"),sQuery(id+"F0.wireOp",EDGE,"E125"),sQuery(id+"F0.wireOp",EDGE,"E126"),sQuery(id+"F0.wireOp",EDGE,"E127"),sQuery(id+"F0.wireOp",EDGE,"E242"),sQuery(id+"F0.wireOp",EDGE,"E243"),sQuery(id+"F0.wireOp",EDGE,"E244"),sQuery(id+"F0.wireOp",EDGE,"E245"),sQuery(id+"F0.wireOp",EDGE,"E246"),sQuery(id+"F0.wireOp",EDGE,"E247"),sQuery(id+"F0.wireOp",EDGE,"E248"),sQuery(id+"F0.wireOp",EDGE,"E249"),sQuery(id+"F0.wireOp",EDGE,"E250"),sQuery(id+"F0.wireOp",EDGE,"E251"),sQuery(id+"F0.wireOp",EDGE,"E252"),sQuery(id+"F0.wireOp",EDGE,"E253"),sQuery(id+"F0.wireOp",EDGE,"E254"),sQuery(id+"F0.wireOp",EDGE,"E255"),sQuery(id+"F0.wireOp",EDGE,"E256"),sQuery(id+"F0.wireOp",EDGE,"E257"),sQuery(id+"F0.wireOp",EDGE,"E258"),sQuery(id+"F0.wireOp",EDGE,"E259"),sQuery(id+"F0.wireOp",EDGE,"E260"),sQuery(id+"F0.wireOp",EDGE,"E261"),sQuery(id+"F0.wireOp",EDGE,"E262"),sQuery(id+"F0.wireOp",EDGE,"E263"),sQuery(id+"F0.wireOp",EDGE,"E264"),sQuery(id+"F0.wireOp",EDGE,"E265"),sQuery(id+"F0.wireOp",EDGE,"E266"),sQuery(id+"F0.wireOp",EDGE,"E267"),sQuery(id+"F0.wireOp",EDGE,"E268"),sQuery(id+"F0.wireOp",EDGE,"E269"),sQuery(id+"F0.wireOp",EDGE,"E270"),sQuery(id+"F0.wireOp",EDGE,"E271")])],"isStart":false})});
            var Q5;
            Q5=makeQuery(id+"F2.boolean.opBoolean","SPLIT",FACE,{"disambiguationData":[TD([makeQuery(id+"F2.opExtrude","SWEPT_FACE",FACE,{"disambiguationData":[OSD([sQuery(id+"F0.wireOp",EDGE,"E140")])]})])],"derivedFrom":makeQuery(id+"F1.opExtrude","CAP_FACE",FACE,{"disambiguationData":[OSD([sQuery(id+"F0.wireOp",EDGE,"E46"),sQuery(id+"F0.wireOp",EDGE,"E47"),sQuery(id+"F0.wireOp",EDGE,"E48"),sQuery(id+"F0.wireOp",EDGE,"E49"),sQuery(id+"F0.wireOp",EDGE,"E50"),sQuery(id+"F0.wireOp",EDGE,"E51"),sQuery(id+"F0.wireOp",EDGE,"E52"),sQuery(id+"F0.wireOp",EDGE,"E53"),sQuery(id+"F0.wireOp",EDGE,"E54"),sQuery(id+"F0.wireOp",EDGE,"E55"),sQuery(id+"F0.wireOp",EDGE,"E56"),sQuery(id+"F0.wireOp",EDGE,"E120"),sQuery(id+"F0.wireOp",EDGE,"E121"),sQuery(id+"F0.wireOp",EDGE,"E122"),sQuery(id+"F0.wireOp",EDGE,"E123"),sQuery(id+"F0.wireOp",EDGE,"E124"),sQuery(id+"F0.wireOp",EDGE,"E125"),sQuery(id+"F0.wireOp",EDGE,"E126"),sQuery(id+"F0.wireOp",EDGE,"E127"),sQuery(id+"F0.wireOp",EDGE,"E242"),sQuery(id+"F0.wireOp",EDGE,"E243"),sQuery(id+"F0.wireOp",EDGE,"E244"),sQuery(id+"F0.wireOp",EDGE,"E245"),sQuery(id+"F0.wireOp",EDGE,"E246"),sQuery(id+"F0.wireOp",EDGE,"E247"),sQuery(id+"F0.wireOp",EDGE,"E248"),sQuery(id+"F0.wireOp",EDGE,"E249"),sQuery(id+"F0.wireOp",EDGE,"E250"),sQuery(id+"F0.wireOp",EDGE,"E251"),sQuery(id+"F0.wireOp",EDGE,"E252"),sQuery(id+"F0.wireOp",EDGE,"E253"),sQuery(id+"F0.wireOp",EDGE,"E254"),sQuery(id+"F0.wireOp",EDGE,"E255"),sQuery(id+"F0.wireOp",EDGE,"E256"),sQuery(id+"F0.wireOp",EDGE,"E257"),sQuery(id+"F0.wireOp",EDGE,"E258"),sQuery(id+"F0.wireOp",EDGE,"E259"),sQuery(id+"F0.wireOp",EDGE,"E260"),sQuery(id+"F0.wireOp",EDGE,"E261"),sQuery(id+"F0.wireOp",EDGE,"E262"),sQuery(id+"F0.wireOp",EDGE,"E263"),sQuery(id+"F0.wireOp",EDGE,"E264"),sQuery(id+"F0.wireOp",EDGE,"E265"),sQuery(id+"F0.wireOp",EDGE,"E266"),sQuery(id+"F0.wireOp",EDGE,"E267"),sQuery(id+"F0.wireOp",EDGE,"E268"),sQuery(id+"F0.wireOp",EDGE,"E269"),sQuery(id+"F0.wireOp",EDGE,"E270"),sQuery(id+"F0.wireOp",EDGE,"E271")])],"isStart":false})});
            var Q6;
            {var subQ0=sQuery(id+"F0.wireOp",EDGE,"E271");var subQ1=sQuery(id+"F0.wireOp",EDGE,"E270");var subQ2=sQuery(id+"F0.wireOp",EDGE,"E269");var subQ3=sQuery(id+"F0.wireOp",EDGE,"E268");var subQ4=sQuery(id+"F0.wireOp",EDGE,"E267");var subQ5=sQuery(id+"F0.wireOp",EDGE,"E266");var subQ6=sQuery(id+"F0.wireOp",EDGE,"E265");var subQ7=sQuery(id+"F0.wireOp",EDGE,"E264");var subQ8=sQuery(id+"F0.wireOp",EDGE,"E251");var subQ9=sQuery(id+"F0.wireOp",EDGE,"E250");var subQ10=sQuery(id+"F0.wireOp",EDGE,"E249");var subQ11=sQuery(id+"F0.wireOp",EDGE,"E248");var subQ12=sQuery(id+"F0.wireOp",EDGE,"E247");var subQ13=sQuery(id+"F0.wireOp",EDGE,"E246");var subQ14=sQuery(id+"F0.wireOp",EDGE,"E242");var subQ15=sQuery(id+"F0.wireOp",EDGE,"E243");var subQ16=sQuery(id+"F0.wireOp",EDGE,"E244");var subQ17=sQuery(id+"F0.wireOp",EDGE,"E245");var subQ18=sQuery(id+"F0.wireOp",EDGE,"E252");var subQ19=sQuery(id+"F0.wireOp",EDGE,"E253");var subQ20=sQuery(id+"F0.wireOp",EDGE,"E254");var subQ21=sQuery(id+"F0.wireOp",EDGE,"E255");var subQ22=sQuery(id+"F0.wireOp",EDGE,"E256");var subQ23=sQuery(id+"F0.wireOp",EDGE,"E257");var subQ24=sQuery(id+"F0.wireOp",EDGE,"E258");var subQ25=sQuery(id+"F0.wireOp",EDGE,"E259");var subQ26=sQuery(id+"F0.wireOp",EDGE,"E260");var subQ27=sQuery(id+"F0.wireOp",EDGE,"E261");var subQ28=sQuery(id+"F0.wireOp",EDGE,"E262");var subQ29=sQuery(id+"F0.wireOp",EDGE,"E263");Q6=makeQuery(id+"F2.boolean.opBoolean","SPLIT",FACE,{"disambiguationData":[TD([makeQuery(id+"F1.opExtrude","SWEPT_FACE",FACE,{"disambiguationData":[OSD([subQ14])]})])],"derivedFrom":makeQuery(id+"F1.opExtrude","CAP_FACE",FACE,{"disambiguationData":[OSD([sQuery(id+"F0.wireOp",EDGE,"E46"),sQuery(id+"F0.wireOp",EDGE,"E47"),sQuery(id+"F0.wireOp",EDGE,"E48"),sQuery(id+"F0.wireOp",EDGE,"E49"),sQuery(id+"F0.wireOp",EDGE,"E50"),sQuery(id+"F0.wireOp",EDGE,"E51"),sQuery(id+"F0.wireOp",EDGE,"E52"),sQuery(id+"F0.wireOp",EDGE,"E53"),sQuery(id+"F0.wireOp",EDGE,"E54"),sQuery(id+"F0.wireOp",EDGE,"E55"),sQuery(id+"F0.wireOp",EDGE,"E56"),sQuery(id+"F0.wireOp",EDGE,"E120"),sQuery(id+"F0.wireOp",EDGE,"E121"),sQuery(id+"F0.wireOp",EDGE,"E122"),sQuery(id+"F0.wireOp",EDGE,"E123"),sQuery(id+"F0.wireOp",EDGE,"E124"),sQuery(id+"F0.wireOp",EDGE,"E125"),sQuery(id+"F0.wireOp",EDGE,"E126"),sQuery(id+"F0.wireOp",EDGE,"E127"),subQ14,subQ15,subQ16,subQ17,subQ13,subQ12,subQ11,subQ10,subQ9,subQ8,subQ18,subQ19,subQ20,subQ21,subQ22,subQ23,subQ24,subQ25,subQ26,subQ27,subQ28,subQ29,subQ7,subQ6,subQ5,subQ4,subQ3,subQ2,subQ1,subQ0])],"isStart":false})});}
            var Q7;
            Q7=makeQuery(id+"F2.opExtrude","CAP_FACE",FACE,{"disambiguationData":[OSD([sQuery(id+"F0.wireOp",EDGE,"E0"),sQuery(id+"F0.wireOp",EDGE,"E1"),sQuery(id+"F0.wireOp",EDGE,"E2"),sQuery(id+"F0.wireOp",EDGE,"E3"),sQuery(id+"F0.wireOp",EDGE,"E4"),sQuery(id+"F0.wireOp",EDGE,"E5"),sQuery(id+"F0.wireOp",EDGE,"E6"),sQuery(id+"F0.wireOp",EDGE,"E7"),sQuery(id+"F0.wireOp",EDGE,"E8"),sQuery(id+"F0.wireOp",EDGE,"E9"),sQuery(id+"F0.wireOp",EDGE,"E10"),sQuery(id+"F0.wireOp",EDGE,"E11"),sQuery(id+"F0.wireOp",EDGE,"E12"),sQuery(id+"F0.wireOp",EDGE,"E13"),sQuery(id+"F0.wireOp",EDGE,"E14"),sQuery(id+"F0.wireOp",EDGE,"E15"),sQuery(id+"F0.wireOp",EDGE,"E16"),sQuery(id+"F0.wireOp",EDGE,"E17"),sQuery(id+"F0.wireOp",EDGE,"E18"),sQuery(id+"F0.wireOp",EDGE,"E19"),sQuery(id+"F0.wireOp",EDGE,"E20"),sQuery(id+"F0.wireOp",EDGE,"E21"),sQuery(id+"F0.wireOp",EDGE,"E22"),sQuery(id+"F0.wireOp",EDGE,"E23"),sQuery(id+"F0.wireOp",EDGE,"E24"),sQuery(id+"F0.wireOp",EDGE,"E25"),sQuery(id+"F0.wireOp",EDGE,"E26"),sQuery(id+"F0.wireOp",EDGE,"E27"),sQuery(id+"F0.wireOp",EDGE,"E28"),sQuery(id+"F0.wireOp",EDGE,"E29"),sQuery(id+"F0.wireOp",EDGE,"E30"),sQuery(id+"F0.wireOp",EDGE,"E31"),sQuery(id+"F0.wireOp",EDGE,"E32"),sQuery(id+"F0.wireOp",EDGE,"E33"),sQuery(id+"F0.wireOp",EDGE,"E34"),sQuery(id+"F0.wireOp",EDGE,"E35"),sQuery(id+"F0.wireOp",EDGE,"E36"),sQuery(id+"F0.wireOp",EDGE,"E37"),sQuery(id+"F0.wireOp",EDGE,"E38"),sQuery(id+"F0.wireOp",EDGE,"E39"),sQuery(id+"F0.wireOp",EDGE,"E40"),sQuery(id+"F0.wireOp",EDGE,"E41")])],"isStart":false});
            extrude(context, id + "F3", {"entities" : qUnion([Q0, Q1, Q2, Q3, Q4, Q5, Q6]), "endBoundEntityFace" : qUnion([Q7]), "depth" : 0.76 * mm});
        }
        {
            var Q0;
            Q0=makeQuery(id+"F1.opExtrude","SWEPT_BODY",BODY,{"disambiguationData":[OSD([sQuery(id+"F0.wireOp",EDGE,"E46"),sQuery(id+"F0.wireOp",EDGE,"E47"),sQuery(id+"F0.wireOp",EDGE,"E48"),sQuery(id+"F0.wireOp",EDGE,"E49"),sQuery(id+"F0.wireOp",EDGE,"E50"),sQuery(id+"F0.wireOp",EDGE,"E51"),sQuery(id+"F0.wireOp",EDGE,"E52"),sQuery(id+"F0.wireOp",EDGE,"E53"),sQuery(id+"F0.wireOp",EDGE,"E54"),sQuery(id+"F0.wireOp",EDGE,"E55"),sQuery(id+"F0.wireOp",EDGE,"E56"),sQuery(id+"F0.wireOp",EDGE,"E120"),sQuery(id+"F0.wireOp",EDGE,"E121"),sQuery(id+"F0.wireOp",EDGE,"E122"),sQuery(id+"F0.wireOp",EDGE,"E123"),sQuery(id+"F0.wireOp",EDGE,"E124"),sQuery(id+"F0.wireOp",EDGE,"E125"),sQuery(id+"F0.wireOp",EDGE,"E126"),sQuery(id+"F0.wireOp",EDGE,"E127"),sQuery(id+"F0.wireOp",EDGE,"E242"),sQuery(id+"F0.wireOp",EDGE,"E243"),sQuery(id+"F0.wireOp",EDGE,"E244"),sQuery(id+"F0.wireOp",EDGE,"E245"),sQuery(id+"F0.wireOp",EDGE,"E246"),sQuery(id+"F0.wireOp",EDGE,"E247"),sQuery(id+"F0.wireOp",EDGE,"E248"),sQuery(id+"F0.wireOp",EDGE,"E249"),sQuery(id+"F0.wireOp",EDGE,"E250"),sQuery(id+"F0.wireOp",EDGE,"E251"),sQuery(id+"F0.wireOp",EDGE,"E252"),sQuery(id+"F0.wireOp",EDGE,"E253"),sQuery(id+"F0.wireOp",EDGE,"E254"),sQuery(id+"F0.wireOp",EDGE,"E255"),sQuery(id+"F0.wireOp",EDGE,"E256"),sQuery(id+"F0.wireOp",EDGE,"E257"),sQuery(id+"F0.wireOp",EDGE,"E258"),sQuery(id+"F0.wireOp",EDGE,"E259"),sQuery(id+"F0.wireOp",EDGE,"E260"),sQuery(id+"F0.wireOp",EDGE,"E261"),sQuery(id+"F0.wireOp",EDGE,"E262"),sQuery(id+"F0.wireOp",EDGE,"E263"),sQuery(id+"F0.wireOp",EDGE,"E264"),sQuery(id+"F0.wireOp",EDGE,"E265"),sQuery(id+"F0.wireOp",EDGE,"E266"),sQuery(id+"F0.wireOp",EDGE,"E267"),sQuery(id+"F0.wireOp",EDGE,"E268"),sQuery(id+"F0.wireOp",EDGE,"E269"),sQuery(id+"F0.wireOp",EDGE,"E270"),sQuery(id+"F0.wireOp",EDGE,"E271")])]});
            var Q1;
            {var subQ0=sQuery(id+"F0.wireOp",EDGE,"E271");var subQ1=sQuery(id+"F0.wireOp",EDGE,"E270");var subQ2=sQuery(id+"F0.wireOp",EDGE,"E269");var subQ3=sQuery(id+"F0.wireOp",EDGE,"E268");var subQ4=sQuery(id+"F0.wireOp",EDGE,"E267");var subQ5=sQuery(id+"F0.wireOp",EDGE,"E266");var subQ6=sQuery(id+"F0.wireOp",EDGE,"E265");var subQ7=sQuery(id+"F0.wireOp",EDGE,"E264");var subQ8=sQuery(id+"F0.wireOp",EDGE,"E263");var subQ9=sQuery(id+"F0.wireOp",EDGE,"E262");var subQ10=sQuery(id+"F0.wireOp",EDGE,"E261");var subQ11=sQuery(id+"F0.wireOp",EDGE,"E260");var subQ12=sQuery(id+"F0.wireOp",EDGE,"E259");var subQ13=sQuery(id+"F0.wireOp",EDGE,"E258");var subQ14=sQuery(id+"F0.wireOp",EDGE,"E257");var subQ15=sQuery(id+"F0.wireOp",EDGE,"E256");var subQ16=sQuery(id+"F0.wireOp",EDGE,"E255");var subQ17=sQuery(id+"F0.wireOp",EDGE,"E254");var subQ18=sQuery(id+"F0.wireOp",EDGE,"E253");var subQ19=sQuery(id+"F0.wireOp",EDGE,"E252");var subQ20=sQuery(id+"F0.wireOp",EDGE,"E251");var subQ21=sQuery(id+"F0.wireOp",EDGE,"E250");var subQ22=sQuery(id+"F0.wireOp",EDGE,"E249");var subQ23=sQuery(id+"F0.wireOp",EDGE,"E248");var subQ24=sQuery(id+"F0.wireOp",EDGE,"E247");var subQ25=sQuery(id+"F0.wireOp",EDGE,"E246");var subQ26=sQuery(id+"F0.wireOp",EDGE,"E245");var subQ27=sQuery(id+"F0.wireOp",EDGE,"E244");var subQ28=sQuery(id+"F0.wireOp",EDGE,"E243");var subQ29=sQuery(id+"F0.wireOp",EDGE,"E242");var subQ30=sQuery(id+"F0.wireOp",EDGE,"E127");var subQ31=sQuery(id+"F0.wireOp",EDGE,"E126");var subQ32=sQuery(id+"F0.wireOp",EDGE,"E125");var subQ33=sQuery(id+"F0.wireOp",EDGE,"E124");var subQ34=sQuery(id+"F0.wireOp",EDGE,"E123");var subQ35=sQuery(id+"F0.wireOp",EDGE,"E122");var subQ36=sQuery(id+"F0.wireOp",EDGE,"E121");var subQ37=sQuery(id+"F0.wireOp",EDGE,"E120");var subQ38=sQuery(id+"F0.wireOp",EDGE,"E56");var subQ39=sQuery(id+"F0.wireOp",EDGE,"E55");var subQ40=sQuery(id+"F0.wireOp",EDGE,"E54");var subQ41=sQuery(id+"F0.wireOp",EDGE,"E53");var subQ42=sQuery(id+"F0.wireOp",EDGE,"E52");var subQ43=sQuery(id+"F0.wireOp",EDGE,"E51");var subQ44=sQuery(id+"F0.wireOp",EDGE,"E50");var subQ45=sQuery(id+"F0.wireOp",EDGE,"E49");var subQ46=sQuery(id+"F0.wireOp",EDGE,"E48");var subQ47=sQuery(id+"F0.wireOp",EDGE,"E47");var subQ48=sQuery(id+"F0.wireOp",EDGE,"E46");Q1=makeQuery(id+"F3.opExtrude","SWEPT_BODY",BODY,{"disambiguationData":[OSD([subQ48,subQ47,subQ46,subQ45,subQ44,subQ43,subQ42,subQ41,subQ40,subQ39,subQ38,subQ37,subQ36,subQ35,subQ34,subQ33,subQ32,subQ31,subQ30,subQ29,subQ28,subQ27,subQ26,subQ25,subQ24,subQ23,subQ22,subQ21,subQ20,subQ19,subQ18,subQ17,subQ16,subQ15,subQ14,subQ13,subQ12,subQ11,subQ10,subQ9,subQ8,subQ7,subQ6,subQ5,subQ4,subQ3,subQ2,subQ1,subQ0]),TDD([makeQuery(id+"F2.boolean.opBoolean","SPLIT",FACE,{"disambiguationData":[TD([makeQuery(id+"F2.opExtrude","SWEPT_FACE",FACE,{"disambiguationData":[OSD([sQuery(id+"F0.wireOp",EDGE,"E42")])]})])],"derivedFrom":makeQuery(id+"F1.opExtrude","CAP_FACE",FACE,{"disambiguationData":[OSD([subQ48,subQ47,subQ46,subQ45,subQ44,subQ43,subQ42,subQ41,subQ40,subQ39,subQ38,subQ37,subQ36,subQ35,subQ34,subQ33,subQ32,subQ31,subQ30,subQ29,subQ28,subQ27,subQ26,subQ25,subQ24,subQ23,subQ22,subQ21,subQ20,subQ19,subQ18,subQ17,subQ16,subQ15,subQ14,subQ13,subQ12,subQ11,subQ10,subQ9,subQ8,subQ7,subQ6,subQ5,subQ4,subQ3,subQ2,subQ1,subQ0])],"isStart":false})})])]});}
            var Q2;
            {var subQ0=sQuery(id+"F0.wireOp",EDGE,"E271");var subQ1=sQuery(id+"F0.wireOp",EDGE,"E270");var subQ2=sQuery(id+"F0.wireOp",EDGE,"E269");var subQ3=sQuery(id+"F0.wireOp",EDGE,"E268");var subQ4=sQuery(id+"F0.wireOp",EDGE,"E267");var subQ5=sQuery(id+"F0.wireOp",EDGE,"E266");var subQ6=sQuery(id+"F0.wireOp",EDGE,"E265");var subQ7=sQuery(id+"F0.wireOp",EDGE,"E264");var subQ8=sQuery(id+"F0.wireOp",EDGE,"E263");var subQ9=sQuery(id+"F0.wireOp",EDGE,"E262");var subQ10=sQuery(id+"F0.wireOp",EDGE,"E261");var subQ11=sQuery(id+"F0.wireOp",EDGE,"E260");var subQ12=sQuery(id+"F0.wireOp",EDGE,"E259");var subQ13=sQuery(id+"F0.wireOp",EDGE,"E258");var subQ14=sQuery(id+"F0.wireOp",EDGE,"E257");var subQ15=sQuery(id+"F0.wireOp",EDGE,"E256");var subQ16=sQuery(id+"F0.wireOp",EDGE,"E255");var subQ17=sQuery(id+"F0.wireOp",EDGE,"E254");var subQ18=sQuery(id+"F0.wireOp",EDGE,"E253");var subQ19=sQuery(id+"F0.wireOp",EDGE,"E252");var subQ20=sQuery(id+"F0.wireOp",EDGE,"E251");var subQ21=sQuery(id+"F0.wireOp",EDGE,"E250");var subQ22=sQuery(id+"F0.wireOp",EDGE,"E249");var subQ23=sQuery(id+"F0.wireOp",EDGE,"E248");var subQ24=sQuery(id+"F0.wireOp",EDGE,"E247");var subQ25=sQuery(id+"F0.wireOp",EDGE,"E246");var subQ26=sQuery(id+"F0.wireOp",EDGE,"E245");var subQ27=sQuery(id+"F0.wireOp",EDGE,"E244");var subQ28=sQuery(id+"F0.wireOp",EDGE,"E243");var subQ29=sQuery(id+"F0.wireOp",EDGE,"E242");var subQ30=sQuery(id+"F0.wireOp",EDGE,"E127");var subQ31=sQuery(id+"F0.wireOp",EDGE,"E126");var subQ32=sQuery(id+"F0.wireOp",EDGE,"E125");var subQ33=sQuery(id+"F0.wireOp",EDGE,"E124");var subQ34=sQuery(id+"F0.wireOp",EDGE,"E123");var subQ35=sQuery(id+"F0.wireOp",EDGE,"E122");var subQ36=sQuery(id+"F0.wireOp",EDGE,"E121");var subQ37=sQuery(id+"F0.wireOp",EDGE,"E120");var subQ38=sQuery(id+"F0.wireOp",EDGE,"E56");var subQ39=sQuery(id+"F0.wireOp",EDGE,"E55");var subQ40=sQuery(id+"F0.wireOp",EDGE,"E54");var subQ41=sQuery(id+"F0.wireOp",EDGE,"E53");var subQ42=sQuery(id+"F0.wireOp",EDGE,"E52");var subQ43=sQuery(id+"F0.wireOp",EDGE,"E51");var subQ44=sQuery(id+"F0.wireOp",EDGE,"E50");var subQ45=sQuery(id+"F0.wireOp",EDGE,"E49");var subQ46=sQuery(id+"F0.wireOp",EDGE,"E48");var subQ47=sQuery(id+"F0.wireOp",EDGE,"E47");var subQ48=sQuery(id+"F0.wireOp",EDGE,"E46");Q2=makeQuery(id+"F3.opExtrude","SWEPT_BODY",BODY,{"disambiguationData":[OSD([subQ48,subQ47,subQ46,subQ45,subQ44,subQ43,subQ42,subQ41,subQ40,subQ39,subQ38,subQ37,subQ36,subQ35,subQ34,subQ33,subQ32,subQ31,subQ30,subQ29,subQ28,subQ27,subQ26,subQ25,subQ24,subQ23,subQ22,subQ21,subQ20,subQ19,subQ18,subQ17,subQ16,subQ15,subQ14,subQ13,subQ12,subQ11,subQ10,subQ9,subQ8,subQ7,subQ6,subQ5,subQ4,subQ3,subQ2,subQ1,subQ0]),TDD([makeQuery(id+"F2.boolean.opBoolean","SPLIT",FACE,{"disambiguationData":[TD([makeQuery(id+"F2.opExtrude","SWEPT_FACE",FACE,{"disambiguationData":[OSD([sQuery(id+"F0.wireOp",EDGE,"E111")])]})])],"derivedFrom":makeQuery(id+"F1.opExtrude","CAP_FACE",FACE,{"disambiguationData":[OSD([subQ48,subQ47,subQ46,subQ45,subQ44,subQ43,subQ42,subQ41,subQ40,subQ39,subQ38,subQ37,subQ36,subQ35,subQ34,subQ33,subQ32,subQ31,subQ30,subQ29,subQ28,subQ27,subQ26,subQ25,subQ24,subQ23,subQ22,subQ21,subQ20,subQ19,subQ18,subQ17,subQ16,subQ15,subQ14,subQ13,subQ12,subQ11,subQ10,subQ9,subQ8,subQ7,subQ6,subQ5,subQ4,subQ3,subQ2,subQ1,subQ0])],"isStart":false})})])]});}
            var Q3;
            {var subQ0=sQuery(id+"F0.wireOp",EDGE,"E271");var subQ1=sQuery(id+"F0.wireOp",EDGE,"E270");var subQ2=sQuery(id+"F0.wireOp",EDGE,"E269");var subQ3=sQuery(id+"F0.wireOp",EDGE,"E268");var subQ4=sQuery(id+"F0.wireOp",EDGE,"E267");var subQ5=sQuery(id+"F0.wireOp",EDGE,"E266");var subQ6=sQuery(id+"F0.wireOp",EDGE,"E265");var subQ7=sQuery(id+"F0.wireOp",EDGE,"E264");var subQ8=sQuery(id+"F0.wireOp",EDGE,"E263");var subQ9=sQuery(id+"F0.wireOp",EDGE,"E262");var subQ10=sQuery(id+"F0.wireOp",EDGE,"E261");var subQ11=sQuery(id+"F0.wireOp",EDGE,"E260");var subQ12=sQuery(id+"F0.wireOp",EDGE,"E259");var subQ13=sQuery(id+"F0.wireOp",EDGE,"E258");var subQ14=sQuery(id+"F0.wireOp",EDGE,"E257");var subQ15=sQuery(id+"F0.wireOp",EDGE,"E256");var subQ16=sQuery(id+"F0.wireOp",EDGE,"E255");var subQ17=sQuery(id+"F0.wireOp",EDGE,"E254");var subQ18=sQuery(id+"F0.wireOp",EDGE,"E253");var subQ19=sQuery(id+"F0.wireOp",EDGE,"E252");var subQ20=sQuery(id+"F0.wireOp",EDGE,"E251");var subQ21=sQuery(id+"F0.wireOp",EDGE,"E250");var subQ22=sQuery(id+"F0.wireOp",EDGE,"E249");var subQ23=sQuery(id+"F0.wireOp",EDGE,"E248");var subQ24=sQuery(id+"F0.wireOp",EDGE,"E247");var subQ25=sQuery(id+"F0.wireOp",EDGE,"E246");var subQ26=sQuery(id+"F0.wireOp",EDGE,"E245");var subQ27=sQuery(id+"F0.wireOp",EDGE,"E244");var subQ28=sQuery(id+"F0.wireOp",EDGE,"E243");var subQ29=sQuery(id+"F0.wireOp",EDGE,"E242");var subQ30=sQuery(id+"F0.wireOp",EDGE,"E127");var subQ31=sQuery(id+"F0.wireOp",EDGE,"E126");var subQ32=sQuery(id+"F0.wireOp",EDGE,"E125");var subQ33=sQuery(id+"F0.wireOp",EDGE,"E124");var subQ34=sQuery(id+"F0.wireOp",EDGE,"E123");var subQ35=sQuery(id+"F0.wireOp",EDGE,"E122");var subQ36=sQuery(id+"F0.wireOp",EDGE,"E121");var subQ37=sQuery(id+"F0.wireOp",EDGE,"E120");var subQ38=sQuery(id+"F0.wireOp",EDGE,"E56");var subQ39=sQuery(id+"F0.wireOp",EDGE,"E55");var subQ40=sQuery(id+"F0.wireOp",EDGE,"E54");var subQ41=sQuery(id+"F0.wireOp",EDGE,"E53");var subQ42=sQuery(id+"F0.wireOp",EDGE,"E52");var subQ43=sQuery(id+"F0.wireOp",EDGE,"E51");var subQ44=sQuery(id+"F0.wireOp",EDGE,"E50");var subQ45=sQuery(id+"F0.wireOp",EDGE,"E49");var subQ46=sQuery(id+"F0.wireOp",EDGE,"E48");var subQ47=sQuery(id+"F0.wireOp",EDGE,"E47");var subQ48=sQuery(id+"F0.wireOp",EDGE,"E46");Q3=makeQuery(id+"F3.opExtrude","SWEPT_BODY",BODY,{"disambiguationData":[OSD([subQ48,subQ47,subQ46,subQ45,subQ44,subQ43,subQ42,subQ41,subQ40,subQ39,subQ38,subQ37,subQ36,subQ35,subQ34,subQ33,subQ32,subQ31,subQ30,subQ29,subQ28,subQ27,subQ26,subQ25,subQ24,subQ23,subQ22,subQ21,subQ20,subQ19,subQ18,subQ17,subQ16,subQ15,subQ14,subQ13,subQ12,subQ11,subQ10,subQ9,subQ8,subQ7,subQ6,subQ5,subQ4,subQ3,subQ2,subQ1,subQ0]),TDD([makeQuery(id+"F2.boolean.opBoolean","SPLIT",FACE,{"disambiguationData":[TD([makeQuery(id+"F2.opExtrude","SWEPT_FACE",FACE,{"disambiguationData":[OSD([sQuery(id+"F0.wireOp",EDGE,"E97")])]})])],"derivedFrom":makeQuery(id+"F1.opExtrude","CAP_FACE",FACE,{"disambiguationData":[OSD([subQ48,subQ47,subQ46,subQ45,subQ44,subQ43,subQ42,subQ41,subQ40,subQ39,subQ38,subQ37,subQ36,subQ35,subQ34,subQ33,subQ32,subQ31,subQ30,subQ29,subQ28,subQ27,subQ26,subQ25,subQ24,subQ23,subQ22,subQ21,subQ20,subQ19,subQ18,subQ17,subQ16,subQ15,subQ14,subQ13,subQ12,subQ11,subQ10,subQ9,subQ8,subQ7,subQ6,subQ5,subQ4,subQ3,subQ2,subQ1,subQ0])],"isStart":false})})])]});}
            var Q4;
            {var subQ0=sQuery(id+"F0.wireOp",EDGE,"E271");var subQ1=sQuery(id+"F0.wireOp",EDGE,"E270");var subQ2=sQuery(id+"F0.wireOp",EDGE,"E269");var subQ3=sQuery(id+"F0.wireOp",EDGE,"E268");var subQ4=sQuery(id+"F0.wireOp",EDGE,"E267");var subQ5=sQuery(id+"F0.wireOp",EDGE,"E266");var subQ6=sQuery(id+"F0.wireOp",EDGE,"E265");var subQ7=sQuery(id+"F0.wireOp",EDGE,"E264");var subQ8=sQuery(id+"F0.wireOp",EDGE,"E263");var subQ9=sQuery(id+"F0.wireOp",EDGE,"E262");var subQ10=sQuery(id+"F0.wireOp",EDGE,"E261");var subQ11=sQuery(id+"F0.wireOp",EDGE,"E260");var subQ12=sQuery(id+"F0.wireOp",EDGE,"E259");var subQ13=sQuery(id+"F0.wireOp",EDGE,"E258");var subQ14=sQuery(id+"F0.wireOp",EDGE,"E257");var subQ15=sQuery(id+"F0.wireOp",EDGE,"E256");var subQ16=sQuery(id+"F0.wireOp",EDGE,"E255");var subQ17=sQuery(id+"F0.wireOp",EDGE,"E254");var subQ18=sQuery(id+"F0.wireOp",EDGE,"E253");var subQ19=sQuery(id+"F0.wireOp",EDGE,"E252");var subQ20=sQuery(id+"F0.wireOp",EDGE,"E251");var subQ21=sQuery(id+"F0.wireOp",EDGE,"E250");var subQ22=sQuery(id+"F0.wireOp",EDGE,"E249");var subQ23=sQuery(id+"F0.wireOp",EDGE,"E248");var subQ24=sQuery(id+"F0.wireOp",EDGE,"E247");var subQ25=sQuery(id+"F0.wireOp",EDGE,"E246");var subQ26=sQuery(id+"F0.wireOp",EDGE,"E245");var subQ27=sQuery(id+"F0.wireOp",EDGE,"E244");var subQ28=sQuery(id+"F0.wireOp",EDGE,"E243");var subQ29=sQuery(id+"F0.wireOp",EDGE,"E242");var subQ30=sQuery(id+"F0.wireOp",EDGE,"E127");var subQ31=sQuery(id+"F0.wireOp",EDGE,"E126");var subQ32=sQuery(id+"F0.wireOp",EDGE,"E125");var subQ33=sQuery(id+"F0.wireOp",EDGE,"E124");var subQ34=sQuery(id+"F0.wireOp",EDGE,"E123");var subQ35=sQuery(id+"F0.wireOp",EDGE,"E122");var subQ36=sQuery(id+"F0.wireOp",EDGE,"E121");var subQ37=sQuery(id+"F0.wireOp",EDGE,"E120");var subQ38=sQuery(id+"F0.wireOp",EDGE,"E56");var subQ39=sQuery(id+"F0.wireOp",EDGE,"E55");var subQ40=sQuery(id+"F0.wireOp",EDGE,"E54");var subQ41=sQuery(id+"F0.wireOp",EDGE,"E53");var subQ42=sQuery(id+"F0.wireOp",EDGE,"E52");var subQ43=sQuery(id+"F0.wireOp",EDGE,"E51");var subQ44=sQuery(id+"F0.wireOp",EDGE,"E50");var subQ45=sQuery(id+"F0.wireOp",EDGE,"E49");var subQ46=sQuery(id+"F0.wireOp",EDGE,"E48");var subQ47=sQuery(id+"F0.wireOp",EDGE,"E47");var subQ48=sQuery(id+"F0.wireOp",EDGE,"E46");Q4=makeQuery(id+"F3.opExtrude","SWEPT_BODY",BODY,{"disambiguationData":[OSD([subQ48,subQ47,subQ46,subQ45,subQ44,subQ43,subQ42,subQ41,subQ40,subQ39,subQ38,subQ37,subQ36,subQ35,subQ34,subQ33,subQ32,subQ31,subQ30,subQ29,subQ28,subQ27,subQ26,subQ25,subQ24,subQ23,subQ22,subQ21,subQ20,subQ19,subQ18,subQ17,subQ16,subQ15,subQ14,subQ13,subQ12,subQ11,subQ10,subQ9,subQ8,subQ7,subQ6,subQ5,subQ4,subQ3,subQ2,subQ1,subQ0]),TDD([makeQuery(id+"F2.boolean.opBoolean","SPLIT",FACE,{"disambiguationData":[TD([makeQuery(id+"F2.opExtrude","SWEPT_FACE",FACE,{"disambiguationData":[OSD([sQuery(id+"F0.wireOp",EDGE,"E57")])]})])],"derivedFrom":makeQuery(id+"F1.opExtrude","CAP_FACE",FACE,{"disambiguationData":[OSD([subQ48,subQ47,subQ46,subQ45,subQ44,subQ43,subQ42,subQ41,subQ40,subQ39,subQ38,subQ37,subQ36,subQ35,subQ34,subQ33,subQ32,subQ31,subQ30,subQ29,subQ28,subQ27,subQ26,subQ25,subQ24,subQ23,subQ22,subQ21,subQ20,subQ19,subQ18,subQ17,subQ16,subQ15,subQ14,subQ13,subQ12,subQ11,subQ10,subQ9,subQ8,subQ7,subQ6,subQ5,subQ4,subQ3,subQ2,subQ1,subQ0])],"isStart":false})})])]});}
            var Q5;
            {var subQ0=sQuery(id+"F0.wireOp",EDGE,"E271");var subQ1=sQuery(id+"F0.wireOp",EDGE,"E270");var subQ2=sQuery(id+"F0.wireOp",EDGE,"E269");var subQ3=sQuery(id+"F0.wireOp",EDGE,"E268");var subQ4=sQuery(id+"F0.wireOp",EDGE,"E267");var subQ5=sQuery(id+"F0.wireOp",EDGE,"E266");var subQ6=sQuery(id+"F0.wireOp",EDGE,"E265");var subQ7=sQuery(id+"F0.wireOp",EDGE,"E264");var subQ8=sQuery(id+"F0.wireOp",EDGE,"E251");var subQ9=sQuery(id+"F0.wireOp",EDGE,"E250");var subQ10=sQuery(id+"F0.wireOp",EDGE,"E249");var subQ11=sQuery(id+"F0.wireOp",EDGE,"E248");var subQ12=sQuery(id+"F0.wireOp",EDGE,"E247");var subQ13=sQuery(id+"F0.wireOp",EDGE,"E246");var subQ14=sQuery(id+"F0.wireOp",EDGE,"E242");var subQ15=sQuery(id+"F0.wireOp",EDGE,"E243");var subQ16=sQuery(id+"F0.wireOp",EDGE,"E244");var subQ17=sQuery(id+"F0.wireOp",EDGE,"E245");var subQ18=sQuery(id+"F0.wireOp",EDGE,"E252");var subQ19=sQuery(id+"F0.wireOp",EDGE,"E253");var subQ20=sQuery(id+"F0.wireOp",EDGE,"E254");var subQ21=sQuery(id+"F0.wireOp",EDGE,"E255");var subQ22=sQuery(id+"F0.wireOp",EDGE,"E256");var subQ23=sQuery(id+"F0.wireOp",EDGE,"E257");var subQ24=sQuery(id+"F0.wireOp",EDGE,"E258");var subQ25=sQuery(id+"F0.wireOp",EDGE,"E259");var subQ26=sQuery(id+"F0.wireOp",EDGE,"E260");var subQ27=sQuery(id+"F0.wireOp",EDGE,"E261");var subQ28=sQuery(id+"F0.wireOp",EDGE,"E262");var subQ29=sQuery(id+"F0.wireOp",EDGE,"E263");var subQ30=sQuery(id+"F0.wireOp",EDGE,"E127");var subQ31=sQuery(id+"F0.wireOp",EDGE,"E126");var subQ32=sQuery(id+"F0.wireOp",EDGE,"E125");var subQ33=sQuery(id+"F0.wireOp",EDGE,"E124");var subQ34=sQuery(id+"F0.wireOp",EDGE,"E123");var subQ35=sQuery(id+"F0.wireOp",EDGE,"E122");var subQ36=sQuery(id+"F0.wireOp",EDGE,"E121");var subQ37=sQuery(id+"F0.wireOp",EDGE,"E120");var subQ38=sQuery(id+"F0.wireOp",EDGE,"E56");var subQ39=sQuery(id+"F0.wireOp",EDGE,"E55");var subQ40=sQuery(id+"F0.wireOp",EDGE,"E54");var subQ41=sQuery(id+"F0.wireOp",EDGE,"E53");var subQ42=sQuery(id+"F0.wireOp",EDGE,"E52");var subQ43=sQuery(id+"F0.wireOp",EDGE,"E51");var subQ44=sQuery(id+"F0.wireOp",EDGE,"E50");var subQ45=sQuery(id+"F0.wireOp",EDGE,"E49");var subQ46=sQuery(id+"F0.wireOp",EDGE,"E48");var subQ47=sQuery(id+"F0.wireOp",EDGE,"E47");var subQ48=sQuery(id+"F0.wireOp",EDGE,"E46");Q5=makeQuery(id+"F3.opExtrude","SWEPT_BODY",BODY,{"disambiguationData":[OSD([subQ48,subQ47,subQ46,subQ45,subQ44,subQ43,subQ42,subQ41,subQ40,subQ39,subQ38,subQ37,subQ36,subQ35,subQ34,subQ33,subQ32,subQ31,subQ30,subQ14,subQ15,subQ16,subQ17,subQ13,subQ12,subQ11,subQ10,subQ9,subQ8,subQ18,subQ19,subQ20,subQ21,subQ22,subQ23,subQ24,subQ25,subQ26,subQ27,subQ28,subQ29,subQ7,subQ6,subQ5,subQ4,subQ3,subQ2,subQ1,subQ0]),TDD([makeQuery(id+"F2.boolean.opBoolean","SPLIT",FACE,{"disambiguationData":[TD([makeQuery(id+"F1.opExtrude","SWEPT_FACE",FACE,{"disambiguationData":[OSD([subQ14])]})])],"derivedFrom":makeQuery(id+"F1.opExtrude","CAP_FACE",FACE,{"disambiguationData":[OSD([subQ48,subQ47,subQ46,subQ45,subQ44,subQ43,subQ42,subQ41,subQ40,subQ39,subQ38,subQ37,subQ36,subQ35,subQ34,subQ33,subQ32,subQ31,subQ30,subQ14,subQ15,subQ16,subQ17,subQ13,subQ12,subQ11,subQ10,subQ9,subQ8,subQ18,subQ19,subQ20,subQ21,subQ22,subQ23,subQ24,subQ25,subQ26,subQ27,subQ28,subQ29,subQ7,subQ6,subQ5,subQ4,subQ3,subQ2,subQ1,subQ0])],"isStart":false})})])]});}
            var Q6;
            {var subQ0=sQuery(id+"F0.wireOp",EDGE,"E271");var subQ1=sQuery(id+"F0.wireOp",EDGE,"E270");var subQ2=sQuery(id+"F0.wireOp",EDGE,"E269");var subQ3=sQuery(id+"F0.wireOp",EDGE,"E268");var subQ4=sQuery(id+"F0.wireOp",EDGE,"E267");var subQ5=sQuery(id+"F0.wireOp",EDGE,"E266");var subQ6=sQuery(id+"F0.wireOp",EDGE,"E265");var subQ7=sQuery(id+"F0.wireOp",EDGE,"E264");var subQ8=sQuery(id+"F0.wireOp",EDGE,"E263");var subQ9=sQuery(id+"F0.wireOp",EDGE,"E262");var subQ10=sQuery(id+"F0.wireOp",EDGE,"E261");var subQ11=sQuery(id+"F0.wireOp",EDGE,"E260");var subQ12=sQuery(id+"F0.wireOp",EDGE,"E259");var subQ13=sQuery(id+"F0.wireOp",EDGE,"E258");var subQ14=sQuery(id+"F0.wireOp",EDGE,"E257");var subQ15=sQuery(id+"F0.wireOp",EDGE,"E256");var subQ16=sQuery(id+"F0.wireOp",EDGE,"E255");var subQ17=sQuery(id+"F0.wireOp",EDGE,"E254");var subQ18=sQuery(id+"F0.wireOp",EDGE,"E253");var subQ19=sQuery(id+"F0.wireOp",EDGE,"E252");var subQ20=sQuery(id+"F0.wireOp",EDGE,"E251");var subQ21=sQuery(id+"F0.wireOp",EDGE,"E250");var subQ22=sQuery(id+"F0.wireOp",EDGE,"E249");var subQ23=sQuery(id+"F0.wireOp",EDGE,"E248");var subQ24=sQuery(id+"F0.wireOp",EDGE,"E247");var subQ25=sQuery(id+"F0.wireOp",EDGE,"E246");var subQ26=sQuery(id+"F0.wireOp",EDGE,"E245");var subQ27=sQuery(id+"F0.wireOp",EDGE,"E244");var subQ28=sQuery(id+"F0.wireOp",EDGE,"E243");var subQ29=sQuery(id+"F0.wireOp",EDGE,"E242");var subQ30=sQuery(id+"F0.wireOp",EDGE,"E127");var subQ31=sQuery(id+"F0.wireOp",EDGE,"E126");var subQ32=sQuery(id+"F0.wireOp",EDGE,"E125");var subQ33=sQuery(id+"F0.wireOp",EDGE,"E124");var subQ34=sQuery(id+"F0.wireOp",EDGE,"E123");var subQ35=sQuery(id+"F0.wireOp",EDGE,"E122");var subQ36=sQuery(id+"F0.wireOp",EDGE,"E121");var subQ37=sQuery(id+"F0.wireOp",EDGE,"E120");var subQ38=sQuery(id+"F0.wireOp",EDGE,"E56");var subQ39=sQuery(id+"F0.wireOp",EDGE,"E55");var subQ40=sQuery(id+"F0.wireOp",EDGE,"E54");var subQ41=sQuery(id+"F0.wireOp",EDGE,"E53");var subQ42=sQuery(id+"F0.wireOp",EDGE,"E52");var subQ43=sQuery(id+"F0.wireOp",EDGE,"E51");var subQ44=sQuery(id+"F0.wireOp",EDGE,"E50");var subQ45=sQuery(id+"F0.wireOp",EDGE,"E49");var subQ46=sQuery(id+"F0.wireOp",EDGE,"E48");var subQ47=sQuery(id+"F0.wireOp",EDGE,"E47");var subQ48=sQuery(id+"F0.wireOp",EDGE,"E46");Q6=makeQuery(id+"F3.opExtrude","SWEPT_BODY",BODY,{"disambiguationData":[OSD([subQ48,subQ47,subQ46,subQ45,subQ44,subQ43,subQ42,subQ41,subQ40,subQ39,subQ38,subQ37,subQ36,subQ35,subQ34,subQ33,subQ32,subQ31,subQ30,subQ29,subQ28,subQ27,subQ26,subQ25,subQ24,subQ23,subQ22,subQ21,subQ20,subQ19,subQ18,subQ17,subQ16,subQ15,subQ14,subQ13,subQ12,subQ11,subQ10,subQ9,subQ8,subQ7,subQ6,subQ5,subQ4,subQ3,subQ2,subQ1,subQ0]),TDD([makeQuery(id+"F2.boolean.opBoolean","SPLIT",FACE,{"disambiguationData":[TD([makeQuery(id+"F2.opExtrude","SWEPT_FACE",FACE,{"disambiguationData":[OSD([sQuery(id+"F0.wireOp",EDGE,"E0")])]})])],"derivedFrom":makeQuery(id+"F1.opExtrude","CAP_FACE",FACE,{"disambiguationData":[OSD([subQ48,subQ47,subQ46,subQ45,subQ44,subQ43,subQ42,subQ41,subQ40,subQ39,subQ38,subQ37,subQ36,subQ35,subQ34,subQ33,subQ32,subQ31,subQ30,subQ29,subQ28,subQ27,subQ26,subQ25,subQ24,subQ23,subQ22,subQ21,subQ20,subQ19,subQ18,subQ17,subQ16,subQ15,subQ14,subQ13,subQ12,subQ11,subQ10,subQ9,subQ8,subQ7,subQ6,subQ5,subQ4,subQ3,subQ2,subQ1,subQ0])],"isStart":false})})])]});}
            var Q7;
            {var subQ0=sQuery(id+"F0.wireOp",EDGE,"E271");var subQ1=sQuery(id+"F0.wireOp",EDGE,"E270");var subQ2=sQuery(id+"F0.wireOp",EDGE,"E269");var subQ3=sQuery(id+"F0.wireOp",EDGE,"E268");var subQ4=sQuery(id+"F0.wireOp",EDGE,"E267");var subQ5=sQuery(id+"F0.wireOp",EDGE,"E266");var subQ6=sQuery(id+"F0.wireOp",EDGE,"E265");var subQ7=sQuery(id+"F0.wireOp",EDGE,"E264");var subQ8=sQuery(id+"F0.wireOp",EDGE,"E263");var subQ9=sQuery(id+"F0.wireOp",EDGE,"E262");var subQ10=sQuery(id+"F0.wireOp",EDGE,"E261");var subQ11=sQuery(id+"F0.wireOp",EDGE,"E260");var subQ12=sQuery(id+"F0.wireOp",EDGE,"E259");var subQ13=sQuery(id+"F0.wireOp",EDGE,"E258");var subQ14=sQuery(id+"F0.wireOp",EDGE,"E257");var subQ15=sQuery(id+"F0.wireOp",EDGE,"E256");var subQ16=sQuery(id+"F0.wireOp",EDGE,"E255");var subQ17=sQuery(id+"F0.wireOp",EDGE,"E254");var subQ18=sQuery(id+"F0.wireOp",EDGE,"E253");var subQ19=sQuery(id+"F0.wireOp",EDGE,"E252");var subQ20=sQuery(id+"F0.wireOp",EDGE,"E251");var subQ21=sQuery(id+"F0.wireOp",EDGE,"E250");var subQ22=sQuery(id+"F0.wireOp",EDGE,"E249");var subQ23=sQuery(id+"F0.wireOp",EDGE,"E248");var subQ24=sQuery(id+"F0.wireOp",EDGE,"E247");var subQ25=sQuery(id+"F0.wireOp",EDGE,"E246");var subQ26=sQuery(id+"F0.wireOp",EDGE,"E245");var subQ27=sQuery(id+"F0.wireOp",EDGE,"E244");var subQ28=sQuery(id+"F0.wireOp",EDGE,"E243");var subQ29=sQuery(id+"F0.wireOp",EDGE,"E242");var subQ30=sQuery(id+"F0.wireOp",EDGE,"E127");var subQ31=sQuery(id+"F0.wireOp",EDGE,"E126");var subQ32=sQuery(id+"F0.wireOp",EDGE,"E125");var subQ33=sQuery(id+"F0.wireOp",EDGE,"E124");var subQ34=sQuery(id+"F0.wireOp",EDGE,"E123");var subQ35=sQuery(id+"F0.wireOp",EDGE,"E122");var subQ36=sQuery(id+"F0.wireOp",EDGE,"E121");var subQ37=sQuery(id+"F0.wireOp",EDGE,"E120");var subQ38=sQuery(id+"F0.wireOp",EDGE,"E56");var subQ39=sQuery(id+"F0.wireOp",EDGE,"E55");var subQ40=sQuery(id+"F0.wireOp",EDGE,"E54");var subQ41=sQuery(id+"F0.wireOp",EDGE,"E53");var subQ42=sQuery(id+"F0.wireOp",EDGE,"E52");var subQ43=sQuery(id+"F0.wireOp",EDGE,"E51");var subQ44=sQuery(id+"F0.wireOp",EDGE,"E50");var subQ45=sQuery(id+"F0.wireOp",EDGE,"E49");var subQ46=sQuery(id+"F0.wireOp",EDGE,"E48");var subQ47=sQuery(id+"F0.wireOp",EDGE,"E47");var subQ48=sQuery(id+"F0.wireOp",EDGE,"E46");Q7=makeQuery(id+"F3.opExtrude","SWEPT_BODY",BODY,{"disambiguationData":[OSD([subQ48,subQ47,subQ46,subQ45,subQ44,subQ43,subQ42,subQ41,subQ40,subQ39,subQ38,subQ37,subQ36,subQ35,subQ34,subQ33,subQ32,subQ31,subQ30,subQ29,subQ28,subQ27,subQ26,subQ25,subQ24,subQ23,subQ22,subQ21,subQ20,subQ19,subQ18,subQ17,subQ16,subQ15,subQ14,subQ13,subQ12,subQ11,subQ10,subQ9,subQ8,subQ7,subQ6,subQ5,subQ4,subQ3,subQ2,subQ1,subQ0]),TDD([makeQuery(id+"F2.boolean.opBoolean","SPLIT",FACE,{"disambiguationData":[TD([makeQuery(id+"F2.opExtrude","SWEPT_FACE",FACE,{"disambiguationData":[OSD([sQuery(id+"F0.wireOp",EDGE,"E140")])]})])],"derivedFrom":makeQuery(id+"F1.opExtrude","CAP_FACE",FACE,{"disambiguationData":[OSD([subQ48,subQ47,subQ46,subQ45,subQ44,subQ43,subQ42,subQ41,subQ40,subQ39,subQ38,subQ37,subQ36,subQ35,subQ34,subQ33,subQ32,subQ31,subQ30,subQ29,subQ28,subQ27,subQ26,subQ25,subQ24,subQ23,subQ22,subQ21,subQ20,subQ19,subQ18,subQ17,subQ16,subQ15,subQ14,subQ13,subQ12,subQ11,subQ10,subQ9,subQ8,subQ7,subQ6,subQ5,subQ4,subQ3,subQ2,subQ1,subQ0])],"isStart":false})})])]});}
            var Q8;
            Q8=qCreatedBy(makeId("Origin.pointOp"),VERTEX);
            transform(context, id + "F4", {"entities" : qUnion([Q0, Q1, Q2, Q3, Q4, Q5, Q6, Q7]), "transformType" : TransformType.SCALE_UNIFORMLY, "scale" : 2.2, "scalePoint" : qUnion([Q8]), "makeCopy" : false});
        }
        {
            var Q0;
            Q0=qCreatedBy(makeId("Front.planeOp"),FACE);
            var sketch = newSketch(context, id + "F5", { "sketchPlane" : qUnion([Q0])});
            skLineSegment(sketch, "E273", {"start": v(0, 0) * mm, "end": v(0, 31.23) * mm});
            skSolve(sketch);
        }
        {
            var Q0;
            Q0=makeQuery(id+"F1.opExtrude","SWEPT_BODY",BODY,{"disambiguationData":[OSD([sQuery(id+"F0.wireOp",EDGE,"E46"),sQuery(id+"F0.wireOp",EDGE,"E47"),sQuery(id+"F0.wireOp",EDGE,"E48"),sQuery(id+"F0.wireOp",EDGE,"E49"),sQuery(id+"F0.wireOp",EDGE,"E50"),sQuery(id+"F0.wireOp",EDGE,"E51"),sQuery(id+"F0.wireOp",EDGE,"E52"),sQuery(id+"F0.wireOp",EDGE,"E53"),sQuery(id+"F0.wireOp",EDGE,"E54"),sQuery(id+"F0.wireOp",EDGE,"E55"),sQuery(id+"F0.wireOp",EDGE,"E56"),sQuery(id+"F0.wireOp",EDGE,"E120"),sQuery(id+"F0.wireOp",EDGE,"E121"),sQuery(id+"F0.wireOp",EDGE,"E122"),sQuery(id+"F0.wireOp",EDGE,"E123"),sQuery(id+"F0.wireOp",EDGE,"E124"),sQuery(id+"F0.wireOp",EDGE,"E125"),sQuery(id+"F0.wireOp",EDGE,"E126"),sQuery(id+"F0.wireOp",EDGE,"E127"),sQuery(id+"F0.wireOp",EDGE,"E242"),sQuery(id+"F0.wireOp",EDGE,"E243"),sQuery(id+"F0.wireOp",EDGE,"E244"),sQuery(id+"F0.wireOp",EDGE,"E245"),sQuery(id+"F0.wireOp",EDGE,"E246"),sQuery(id+"F0.wireOp",EDGE,"E247"),sQuery(id+"F0.wireOp",EDGE,"E248"),sQuery(id+"F0.wireOp",EDGE,"E249"),sQuery(id+"F0.wireOp",EDGE,"E250"),sQuery(id+"F0.wireOp",EDGE,"E251"),sQuery(id+"F0.wireOp",EDGE,"E252"),sQuery(id+"F0.wireOp",EDGE,"E253"),sQuery(id+"F0.wireOp",EDGE,"E254"),sQuery(id+"F0.wireOp",EDGE,"E255"),sQuery(id+"F0.wireOp",EDGE,"E256"),sQuery(id+"F0.wireOp",EDGE,"E257"),sQuery(id+"F0.wireOp",EDGE,"E258"),sQuery(id+"F0.wireOp",EDGE,"E259"),sQuery(id+"F0.wireOp",EDGE,"E260"),sQuery(id+"F0.wireOp",EDGE,"E261"),sQuery(id+"F0.wireOp",EDGE,"E262"),sQuery(id+"F0.wireOp",EDGE,"E263"),sQuery(id+"F0.wireOp",EDGE,"E264"),sQuery(id+"F0.wireOp",EDGE,"E265"),sQuery(id+"F0.wireOp",EDGE,"E266"),sQuery(id+"F0.wireOp",EDGE,"E267"),sQuery(id+"F0.wireOp",EDGE,"E268"),sQuery(id+"F0.wireOp",EDGE,"E269"),sQuery(id+"F0.wireOp",EDGE,"E270"),sQuery(id+"F0.wireOp",EDGE,"E271")])]});
            var Q1;
            {var subQ0=sQuery(id+"F0.wireOp",EDGE,"E271");var subQ1=sQuery(id+"F0.wireOp",EDGE,"E270");var subQ2=sQuery(id+"F0.wireOp",EDGE,"E269");var subQ3=sQuery(id+"F0.wireOp",EDGE,"E268");var subQ4=sQuery(id+"F0.wireOp",EDGE,"E267");var subQ5=sQuery(id+"F0.wireOp",EDGE,"E266");var subQ6=sQuery(id+"F0.wireOp",EDGE,"E265");var subQ7=sQuery(id+"F0.wireOp",EDGE,"E264");var subQ8=sQuery(id+"F0.wireOp",EDGE,"E263");var subQ9=sQuery(id+"F0.wireOp",EDGE,"E262");var subQ10=sQuery(id+"F0.wireOp",EDGE,"E261");var subQ11=sQuery(id+"F0.wireOp",EDGE,"E260");var subQ12=sQuery(id+"F0.wireOp",EDGE,"E259");var subQ13=sQuery(id+"F0.wireOp",EDGE,"E258");var subQ14=sQuery(id+"F0.wireOp",EDGE,"E257");var subQ15=sQuery(id+"F0.wireOp",EDGE,"E256");var subQ16=sQuery(id+"F0.wireOp",EDGE,"E255");var subQ17=sQuery(id+"F0.wireOp",EDGE,"E254");var subQ18=sQuery(id+"F0.wireOp",EDGE,"E253");var subQ19=sQuery(id+"F0.wireOp",EDGE,"E252");var subQ20=sQuery(id+"F0.wireOp",EDGE,"E251");var subQ21=sQuery(id+"F0.wireOp",EDGE,"E250");var subQ22=sQuery(id+"F0.wireOp",EDGE,"E249");var subQ23=sQuery(id+"F0.wireOp",EDGE,"E248");var subQ24=sQuery(id+"F0.wireOp",EDGE,"E247");var subQ25=sQuery(id+"F0.wireOp",EDGE,"E246");var subQ26=sQuery(id+"F0.wireOp",EDGE,"E245");var subQ27=sQuery(id+"F0.wireOp",EDGE,"E244");var subQ28=sQuery(id+"F0.wireOp",EDGE,"E243");var subQ29=sQuery(id+"F0.wireOp",EDGE,"E242");var subQ30=sQuery(id+"F0.wireOp",EDGE,"E127");var subQ31=sQuery(id+"F0.wireOp",EDGE,"E126");var subQ32=sQuery(id+"F0.wireOp",EDGE,"E125");var subQ33=sQuery(id+"F0.wireOp",EDGE,"E124");var subQ34=sQuery(id+"F0.wireOp",EDGE,"E123");var subQ35=sQuery(id+"F0.wireOp",EDGE,"E122");var subQ36=sQuery(id+"F0.wireOp",EDGE,"E121");var subQ37=sQuery(id+"F0.wireOp",EDGE,"E120");var subQ38=sQuery(id+"F0.wireOp",EDGE,"E56");var subQ39=sQuery(id+"F0.wireOp",EDGE,"E55");var subQ40=sQuery(id+"F0.wireOp",EDGE,"E54");var subQ41=sQuery(id+"F0.wireOp",EDGE,"E53");var subQ42=sQuery(id+"F0.wireOp",EDGE,"E52");var subQ43=sQuery(id+"F0.wireOp",EDGE,"E51");var subQ44=sQuery(id+"F0.wireOp",EDGE,"E50");var subQ45=sQuery(id+"F0.wireOp",EDGE,"E49");var subQ46=sQuery(id+"F0.wireOp",EDGE,"E48");var subQ47=sQuery(id+"F0.wireOp",EDGE,"E47");var subQ48=sQuery(id+"F0.wireOp",EDGE,"E46");Q1=makeQuery(id+"F3.opExtrude","SWEPT_BODY",BODY,{"disambiguationData":[OSD([subQ48,subQ47,subQ46,subQ45,subQ44,subQ43,subQ42,subQ41,subQ40,subQ39,subQ38,subQ37,subQ36,subQ35,subQ34,subQ33,subQ32,subQ31,subQ30,subQ29,subQ28,subQ27,subQ26,subQ25,subQ24,subQ23,subQ22,subQ21,subQ20,subQ19,subQ18,subQ17,subQ16,subQ15,subQ14,subQ13,subQ12,subQ11,subQ10,subQ9,subQ8,subQ7,subQ6,subQ5,subQ4,subQ3,subQ2,subQ1,subQ0]),TDD([makeQuery(id+"F2.boolean.opBoolean","SPLIT",FACE,{"disambiguationData":[TD([makeQuery(id+"F2.opExtrude","SWEPT_FACE",FACE,{"disambiguationData":[OSD([sQuery(id+"F0.wireOp",EDGE,"E42")])]})])],"derivedFrom":makeQuery(id+"F1.opExtrude","CAP_FACE",FACE,{"disambiguationData":[OSD([subQ48,subQ47,subQ46,subQ45,subQ44,subQ43,subQ42,subQ41,subQ40,subQ39,subQ38,subQ37,subQ36,subQ35,subQ34,subQ33,subQ32,subQ31,subQ30,subQ29,subQ28,subQ27,subQ26,subQ25,subQ24,subQ23,subQ22,subQ21,subQ20,subQ19,subQ18,subQ17,subQ16,subQ15,subQ14,subQ13,subQ12,subQ11,subQ10,subQ9,subQ8,subQ7,subQ6,subQ5,subQ4,subQ3,subQ2,subQ1,subQ0])],"isStart":false})})])]});}
            var Q2;
            {var subQ0=sQuery(id+"F0.wireOp",EDGE,"E271");var subQ1=sQuery(id+"F0.wireOp",EDGE,"E270");var subQ2=sQuery(id+"F0.wireOp",EDGE,"E269");var subQ3=sQuery(id+"F0.wireOp",EDGE,"E268");var subQ4=sQuery(id+"F0.wireOp",EDGE,"E267");var subQ5=sQuery(id+"F0.wireOp",EDGE,"E266");var subQ6=sQuery(id+"F0.wireOp",EDGE,"E265");var subQ7=sQuery(id+"F0.wireOp",EDGE,"E264");var subQ8=sQuery(id+"F0.wireOp",EDGE,"E263");var subQ9=sQuery(id+"F0.wireOp",EDGE,"E262");var subQ10=sQuery(id+"F0.wireOp",EDGE,"E261");var subQ11=sQuery(id+"F0.wireOp",EDGE,"E260");var subQ12=sQuery(id+"F0.wireOp",EDGE,"E259");var subQ13=sQuery(id+"F0.wireOp",EDGE,"E258");var subQ14=sQuery(id+"F0.wireOp",EDGE,"E257");var subQ15=sQuery(id+"F0.wireOp",EDGE,"E256");var subQ16=sQuery(id+"F0.wireOp",EDGE,"E255");var subQ17=sQuery(id+"F0.wireOp",EDGE,"E254");var subQ18=sQuery(id+"F0.wireOp",EDGE,"E253");var subQ19=sQuery(id+"F0.wireOp",EDGE,"E252");var subQ20=sQuery(id+"F0.wireOp",EDGE,"E251");var subQ21=sQuery(id+"F0.wireOp",EDGE,"E250");var subQ22=sQuery(id+"F0.wireOp",EDGE,"E249");var subQ23=sQuery(id+"F0.wireOp",EDGE,"E248");var subQ24=sQuery(id+"F0.wireOp",EDGE,"E247");var subQ25=sQuery(id+"F0.wireOp",EDGE,"E246");var subQ26=sQuery(id+"F0.wireOp",EDGE,"E245");var subQ27=sQuery(id+"F0.wireOp",EDGE,"E244");var subQ28=sQuery(id+"F0.wireOp",EDGE,"E243");var subQ29=sQuery(id+"F0.wireOp",EDGE,"E242");var subQ30=sQuery(id+"F0.wireOp",EDGE,"E127");var subQ31=sQuery(id+"F0.wireOp",EDGE,"E126");var subQ32=sQuery(id+"F0.wireOp",EDGE,"E125");var subQ33=sQuery(id+"F0.wireOp",EDGE,"E124");var subQ34=sQuery(id+"F0.wireOp",EDGE,"E123");var subQ35=sQuery(id+"F0.wireOp",EDGE,"E122");var subQ36=sQuery(id+"F0.wireOp",EDGE,"E121");var subQ37=sQuery(id+"F0.wireOp",EDGE,"E120");var subQ38=sQuery(id+"F0.wireOp",EDGE,"E56");var subQ39=sQuery(id+"F0.wireOp",EDGE,"E55");var subQ40=sQuery(id+"F0.wireOp",EDGE,"E54");var subQ41=sQuery(id+"F0.wireOp",EDGE,"E53");var subQ42=sQuery(id+"F0.wireOp",EDGE,"E52");var subQ43=sQuery(id+"F0.wireOp",EDGE,"E51");var subQ44=sQuery(id+"F0.wireOp",EDGE,"E50");var subQ45=sQuery(id+"F0.wireOp",EDGE,"E49");var subQ46=sQuery(id+"F0.wireOp",EDGE,"E48");var subQ47=sQuery(id+"F0.wireOp",EDGE,"E47");var subQ48=sQuery(id+"F0.wireOp",EDGE,"E46");Q2=makeQuery(id+"F3.opExtrude","SWEPT_BODY",BODY,{"disambiguationData":[OSD([subQ48,subQ47,subQ46,subQ45,subQ44,subQ43,subQ42,subQ41,subQ40,subQ39,subQ38,subQ37,subQ36,subQ35,subQ34,subQ33,subQ32,subQ31,subQ30,subQ29,subQ28,subQ27,subQ26,subQ25,subQ24,subQ23,subQ22,subQ21,subQ20,subQ19,subQ18,subQ17,subQ16,subQ15,subQ14,subQ13,subQ12,subQ11,subQ10,subQ9,subQ8,subQ7,subQ6,subQ5,subQ4,subQ3,subQ2,subQ1,subQ0]),TDD([makeQuery(id+"F2.boolean.opBoolean","SPLIT",FACE,{"disambiguationData":[TD([makeQuery(id+"F2.opExtrude","SWEPT_FACE",FACE,{"disambiguationData":[OSD([sQuery(id+"F0.wireOp",EDGE,"E111")])]})])],"derivedFrom":makeQuery(id+"F1.opExtrude","CAP_FACE",FACE,{"disambiguationData":[OSD([subQ48,subQ47,subQ46,subQ45,subQ44,subQ43,subQ42,subQ41,subQ40,subQ39,subQ38,subQ37,subQ36,subQ35,subQ34,subQ33,subQ32,subQ31,subQ30,subQ29,subQ28,subQ27,subQ26,subQ25,subQ24,subQ23,subQ22,subQ21,subQ20,subQ19,subQ18,subQ17,subQ16,subQ15,subQ14,subQ13,subQ12,subQ11,subQ10,subQ9,subQ8,subQ7,subQ6,subQ5,subQ4,subQ3,subQ2,subQ1,subQ0])],"isStart":false})})])]});}
            var Q3;
            {var subQ0=sQuery(id+"F0.wireOp",EDGE,"E271");var subQ1=sQuery(id+"F0.wireOp",EDGE,"E270");var subQ2=sQuery(id+"F0.wireOp",EDGE,"E269");var subQ3=sQuery(id+"F0.wireOp",EDGE,"E268");var subQ4=sQuery(id+"F0.wireOp",EDGE,"E267");var subQ5=sQuery(id+"F0.wireOp",EDGE,"E266");var subQ6=sQuery(id+"F0.wireOp",EDGE,"E265");var subQ7=sQuery(id+"F0.wireOp",EDGE,"E264");var subQ8=sQuery(id+"F0.wireOp",EDGE,"E263");var subQ9=sQuery(id+"F0.wireOp",EDGE,"E262");var subQ10=sQuery(id+"F0.wireOp",EDGE,"E261");var subQ11=sQuery(id+"F0.wireOp",EDGE,"E260");var subQ12=sQuery(id+"F0.wireOp",EDGE,"E259");var subQ13=sQuery(id+"F0.wireOp",EDGE,"E258");var subQ14=sQuery(id+"F0.wireOp",EDGE,"E257");var subQ15=sQuery(id+"F0.wireOp",EDGE,"E256");var subQ16=sQuery(id+"F0.wireOp",EDGE,"E255");var subQ17=sQuery(id+"F0.wireOp",EDGE,"E254");var subQ18=sQuery(id+"F0.wireOp",EDGE,"E253");var subQ19=sQuery(id+"F0.wireOp",EDGE,"E252");var subQ20=sQuery(id+"F0.wireOp",EDGE,"E251");var subQ21=sQuery(id+"F0.wireOp",EDGE,"E250");var subQ22=sQuery(id+"F0.wireOp",EDGE,"E249");var subQ23=sQuery(id+"F0.wireOp",EDGE,"E248");var subQ24=sQuery(id+"F0.wireOp",EDGE,"E247");var subQ25=sQuery(id+"F0.wireOp",EDGE,"E246");var subQ26=sQuery(id+"F0.wireOp",EDGE,"E245");var subQ27=sQuery(id+"F0.wireOp",EDGE,"E244");var subQ28=sQuery(id+"F0.wireOp",EDGE,"E243");var subQ29=sQuery(id+"F0.wireOp",EDGE,"E242");var subQ30=sQuery(id+"F0.wireOp",EDGE,"E127");var subQ31=sQuery(id+"F0.wireOp",EDGE,"E126");var subQ32=sQuery(id+"F0.wireOp",EDGE,"E125");var subQ33=sQuery(id+"F0.wireOp",EDGE,"E124");var subQ34=sQuery(id+"F0.wireOp",EDGE,"E123");var subQ35=sQuery(id+"F0.wireOp",EDGE,"E122");var subQ36=sQuery(id+"F0.wireOp",EDGE,"E121");var subQ37=sQuery(id+"F0.wireOp",EDGE,"E120");var subQ38=sQuery(id+"F0.wireOp",EDGE,"E56");var subQ39=sQuery(id+"F0.wireOp",EDGE,"E55");var subQ40=sQuery(id+"F0.wireOp",EDGE,"E54");var subQ41=sQuery(id+"F0.wireOp",EDGE,"E53");var subQ42=sQuery(id+"F0.wireOp",EDGE,"E52");var subQ43=sQuery(id+"F0.wireOp",EDGE,"E51");var subQ44=sQuery(id+"F0.wireOp",EDGE,"E50");var subQ45=sQuery(id+"F0.wireOp",EDGE,"E49");var subQ46=sQuery(id+"F0.wireOp",EDGE,"E48");var subQ47=sQuery(id+"F0.wireOp",EDGE,"E47");var subQ48=sQuery(id+"F0.wireOp",EDGE,"E46");Q3=makeQuery(id+"F3.opExtrude","SWEPT_BODY",BODY,{"disambiguationData":[OSD([subQ48,subQ47,subQ46,subQ45,subQ44,subQ43,subQ42,subQ41,subQ40,subQ39,subQ38,subQ37,subQ36,subQ35,subQ34,subQ33,subQ32,subQ31,subQ30,subQ29,subQ28,subQ27,subQ26,subQ25,subQ24,subQ23,subQ22,subQ21,subQ20,subQ19,subQ18,subQ17,subQ16,subQ15,subQ14,subQ13,subQ12,subQ11,subQ10,subQ9,subQ8,subQ7,subQ6,subQ5,subQ4,subQ3,subQ2,subQ1,subQ0]),TDD([makeQuery(id+"F2.boolean.opBoolean","SPLIT",FACE,{"disambiguationData":[TD([makeQuery(id+"F2.opExtrude","SWEPT_FACE",FACE,{"disambiguationData":[OSD([sQuery(id+"F0.wireOp",EDGE,"E97")])]})])],"derivedFrom":makeQuery(id+"F1.opExtrude","CAP_FACE",FACE,{"disambiguationData":[OSD([subQ48,subQ47,subQ46,subQ45,subQ44,subQ43,subQ42,subQ41,subQ40,subQ39,subQ38,subQ37,subQ36,subQ35,subQ34,subQ33,subQ32,subQ31,subQ30,subQ29,subQ28,subQ27,subQ26,subQ25,subQ24,subQ23,subQ22,subQ21,subQ20,subQ19,subQ18,subQ17,subQ16,subQ15,subQ14,subQ13,subQ12,subQ11,subQ10,subQ9,subQ8,subQ7,subQ6,subQ5,subQ4,subQ3,subQ2,subQ1,subQ0])],"isStart":false})})])]});}
            var Q4;
            {var subQ0=sQuery(id+"F0.wireOp",EDGE,"E271");var subQ1=sQuery(id+"F0.wireOp",EDGE,"E270");var subQ2=sQuery(id+"F0.wireOp",EDGE,"E269");var subQ3=sQuery(id+"F0.wireOp",EDGE,"E268");var subQ4=sQuery(id+"F0.wireOp",EDGE,"E267");var subQ5=sQuery(id+"F0.wireOp",EDGE,"E266");var subQ6=sQuery(id+"F0.wireOp",EDGE,"E265");var subQ7=sQuery(id+"F0.wireOp",EDGE,"E264");var subQ8=sQuery(id+"F0.wireOp",EDGE,"E263");var subQ9=sQuery(id+"F0.wireOp",EDGE,"E262");var subQ10=sQuery(id+"F0.wireOp",EDGE,"E261");var subQ11=sQuery(id+"F0.wireOp",EDGE,"E260");var subQ12=sQuery(id+"F0.wireOp",EDGE,"E259");var subQ13=sQuery(id+"F0.wireOp",EDGE,"E258");var subQ14=sQuery(id+"F0.wireOp",EDGE,"E257");var subQ15=sQuery(id+"F0.wireOp",EDGE,"E256");var subQ16=sQuery(id+"F0.wireOp",EDGE,"E255");var subQ17=sQuery(id+"F0.wireOp",EDGE,"E254");var subQ18=sQuery(id+"F0.wireOp",EDGE,"E253");var subQ19=sQuery(id+"F0.wireOp",EDGE,"E252");var subQ20=sQuery(id+"F0.wireOp",EDGE,"E251");var subQ21=sQuery(id+"F0.wireOp",EDGE,"E250");var subQ22=sQuery(id+"F0.wireOp",EDGE,"E249");var subQ23=sQuery(id+"F0.wireOp",EDGE,"E248");var subQ24=sQuery(id+"F0.wireOp",EDGE,"E247");var subQ25=sQuery(id+"F0.wireOp",EDGE,"E246");var subQ26=sQuery(id+"F0.wireOp",EDGE,"E245");var subQ27=sQuery(id+"F0.wireOp",EDGE,"E244");var subQ28=sQuery(id+"F0.wireOp",EDGE,"E243");var subQ29=sQuery(id+"F0.wireOp",EDGE,"E242");var subQ30=sQuery(id+"F0.wireOp",EDGE,"E127");var subQ31=sQuery(id+"F0.wireOp",EDGE,"E126");var subQ32=sQuery(id+"F0.wireOp",EDGE,"E125");var subQ33=sQuery(id+"F0.wireOp",EDGE,"E124");var subQ34=sQuery(id+"F0.wireOp",EDGE,"E123");var subQ35=sQuery(id+"F0.wireOp",EDGE,"E122");var subQ36=sQuery(id+"F0.wireOp",EDGE,"E121");var subQ37=sQuery(id+"F0.wireOp",EDGE,"E120");var subQ38=sQuery(id+"F0.wireOp",EDGE,"E56");var subQ39=sQuery(id+"F0.wireOp",EDGE,"E55");var subQ40=sQuery(id+"F0.wireOp",EDGE,"E54");var subQ41=sQuery(id+"F0.wireOp",EDGE,"E53");var subQ42=sQuery(id+"F0.wireOp",EDGE,"E52");var subQ43=sQuery(id+"F0.wireOp",EDGE,"E51");var subQ44=sQuery(id+"F0.wireOp",EDGE,"E50");var subQ45=sQuery(id+"F0.wireOp",EDGE,"E49");var subQ46=sQuery(id+"F0.wireOp",EDGE,"E48");var subQ47=sQuery(id+"F0.wireOp",EDGE,"E47");var subQ48=sQuery(id+"F0.wireOp",EDGE,"E46");Q4=makeQuery(id+"F3.opExtrude","SWEPT_BODY",BODY,{"disambiguationData":[OSD([subQ48,subQ47,subQ46,subQ45,subQ44,subQ43,subQ42,subQ41,subQ40,subQ39,subQ38,subQ37,subQ36,subQ35,subQ34,subQ33,subQ32,subQ31,subQ30,subQ29,subQ28,subQ27,subQ26,subQ25,subQ24,subQ23,subQ22,subQ21,subQ20,subQ19,subQ18,subQ17,subQ16,subQ15,subQ14,subQ13,subQ12,subQ11,subQ10,subQ9,subQ8,subQ7,subQ6,subQ5,subQ4,subQ3,subQ2,subQ1,subQ0]),TDD([makeQuery(id+"F2.boolean.opBoolean","SPLIT",FACE,{"disambiguationData":[TD([makeQuery(id+"F2.opExtrude","SWEPT_FACE",FACE,{"disambiguationData":[OSD([sQuery(id+"F0.wireOp",EDGE,"E57")])]})])],"derivedFrom":makeQuery(id+"F1.opExtrude","CAP_FACE",FACE,{"disambiguationData":[OSD([subQ48,subQ47,subQ46,subQ45,subQ44,subQ43,subQ42,subQ41,subQ40,subQ39,subQ38,subQ37,subQ36,subQ35,subQ34,subQ33,subQ32,subQ31,subQ30,subQ29,subQ28,subQ27,subQ26,subQ25,subQ24,subQ23,subQ22,subQ21,subQ20,subQ19,subQ18,subQ17,subQ16,subQ15,subQ14,subQ13,subQ12,subQ11,subQ10,subQ9,subQ8,subQ7,subQ6,subQ5,subQ4,subQ3,subQ2,subQ1,subQ0])],"isStart":false})})])]});}
            var Q5;
            {var subQ0=sQuery(id+"F0.wireOp",EDGE,"E271");var subQ1=sQuery(id+"F0.wireOp",EDGE,"E270");var subQ2=sQuery(id+"F0.wireOp",EDGE,"E269");var subQ3=sQuery(id+"F0.wireOp",EDGE,"E268");var subQ4=sQuery(id+"F0.wireOp",EDGE,"E267");var subQ5=sQuery(id+"F0.wireOp",EDGE,"E266");var subQ6=sQuery(id+"F0.wireOp",EDGE,"E265");var subQ7=sQuery(id+"F0.wireOp",EDGE,"E264");var subQ8=sQuery(id+"F0.wireOp",EDGE,"E251");var subQ9=sQuery(id+"F0.wireOp",EDGE,"E250");var subQ10=sQuery(id+"F0.wireOp",EDGE,"E249");var subQ11=sQuery(id+"F0.wireOp",EDGE,"E248");var subQ12=sQuery(id+"F0.wireOp",EDGE,"E247");var subQ13=sQuery(id+"F0.wireOp",EDGE,"E246");var subQ14=sQuery(id+"F0.wireOp",EDGE,"E242");var subQ15=sQuery(id+"F0.wireOp",EDGE,"E243");var subQ16=sQuery(id+"F0.wireOp",EDGE,"E244");var subQ17=sQuery(id+"F0.wireOp",EDGE,"E245");var subQ18=sQuery(id+"F0.wireOp",EDGE,"E252");var subQ19=sQuery(id+"F0.wireOp",EDGE,"E253");var subQ20=sQuery(id+"F0.wireOp",EDGE,"E254");var subQ21=sQuery(id+"F0.wireOp",EDGE,"E255");var subQ22=sQuery(id+"F0.wireOp",EDGE,"E256");var subQ23=sQuery(id+"F0.wireOp",EDGE,"E257");var subQ24=sQuery(id+"F0.wireOp",EDGE,"E258");var subQ25=sQuery(id+"F0.wireOp",EDGE,"E259");var subQ26=sQuery(id+"F0.wireOp",EDGE,"E260");var subQ27=sQuery(id+"F0.wireOp",EDGE,"E261");var subQ28=sQuery(id+"F0.wireOp",EDGE,"E262");var subQ29=sQuery(id+"F0.wireOp",EDGE,"E263");var subQ30=sQuery(id+"F0.wireOp",EDGE,"E127");var subQ31=sQuery(id+"F0.wireOp",EDGE,"E126");var subQ32=sQuery(id+"F0.wireOp",EDGE,"E125");var subQ33=sQuery(id+"F0.wireOp",EDGE,"E124");var subQ34=sQuery(id+"F0.wireOp",EDGE,"E123");var subQ35=sQuery(id+"F0.wireOp",EDGE,"E122");var subQ36=sQuery(id+"F0.wireOp",EDGE,"E121");var subQ37=sQuery(id+"F0.wireOp",EDGE,"E120");var subQ38=sQuery(id+"F0.wireOp",EDGE,"E56");var subQ39=sQuery(id+"F0.wireOp",EDGE,"E55");var subQ40=sQuery(id+"F0.wireOp",EDGE,"E54");var subQ41=sQuery(id+"F0.wireOp",EDGE,"E53");var subQ42=sQuery(id+"F0.wireOp",EDGE,"E52");var subQ43=sQuery(id+"F0.wireOp",EDGE,"E51");var subQ44=sQuery(id+"F0.wireOp",EDGE,"E50");var subQ45=sQuery(id+"F0.wireOp",EDGE,"E49");var subQ46=sQuery(id+"F0.wireOp",EDGE,"E48");var subQ47=sQuery(id+"F0.wireOp",EDGE,"E47");var subQ48=sQuery(id+"F0.wireOp",EDGE,"E46");Q5=makeQuery(id+"F3.opExtrude","SWEPT_BODY",BODY,{"disambiguationData":[OSD([subQ48,subQ47,subQ46,subQ45,subQ44,subQ43,subQ42,subQ41,subQ40,subQ39,subQ38,subQ37,subQ36,subQ35,subQ34,subQ33,subQ32,subQ31,subQ30,subQ14,subQ15,subQ16,subQ17,subQ13,subQ12,subQ11,subQ10,subQ9,subQ8,subQ18,subQ19,subQ20,subQ21,subQ22,subQ23,subQ24,subQ25,subQ26,subQ27,subQ28,subQ29,subQ7,subQ6,subQ5,subQ4,subQ3,subQ2,subQ1,subQ0]),TDD([makeQuery(id+"F2.boolean.opBoolean","SPLIT",FACE,{"disambiguationData":[TD([makeQuery(id+"F1.opExtrude","SWEPT_FACE",FACE,{"disambiguationData":[OSD([subQ14])]})])],"derivedFrom":makeQuery(id+"F1.opExtrude","CAP_FACE",FACE,{"disambiguationData":[OSD([subQ48,subQ47,subQ46,subQ45,subQ44,subQ43,subQ42,subQ41,subQ40,subQ39,subQ38,subQ37,subQ36,subQ35,subQ34,subQ33,subQ32,subQ31,subQ30,subQ14,subQ15,subQ16,subQ17,subQ13,subQ12,subQ11,subQ10,subQ9,subQ8,subQ18,subQ19,subQ20,subQ21,subQ22,subQ23,subQ24,subQ25,subQ26,subQ27,subQ28,subQ29,subQ7,subQ6,subQ5,subQ4,subQ3,subQ2,subQ1,subQ0])],"isStart":false})})])]});}
            var Q6;
            {var subQ0=sQuery(id+"F0.wireOp",EDGE,"E271");var subQ1=sQuery(id+"F0.wireOp",EDGE,"E270");var subQ2=sQuery(id+"F0.wireOp",EDGE,"E269");var subQ3=sQuery(id+"F0.wireOp",EDGE,"E268");var subQ4=sQuery(id+"F0.wireOp",EDGE,"E267");var subQ5=sQuery(id+"F0.wireOp",EDGE,"E266");var subQ6=sQuery(id+"F0.wireOp",EDGE,"E265");var subQ7=sQuery(id+"F0.wireOp",EDGE,"E264");var subQ8=sQuery(id+"F0.wireOp",EDGE,"E263");var subQ9=sQuery(id+"F0.wireOp",EDGE,"E262");var subQ10=sQuery(id+"F0.wireOp",EDGE,"E261");var subQ11=sQuery(id+"F0.wireOp",EDGE,"E260");var subQ12=sQuery(id+"F0.wireOp",EDGE,"E259");var subQ13=sQuery(id+"F0.wireOp",EDGE,"E258");var subQ14=sQuery(id+"F0.wireOp",EDGE,"E257");var subQ15=sQuery(id+"F0.wireOp",EDGE,"E256");var subQ16=sQuery(id+"F0.wireOp",EDGE,"E255");var subQ17=sQuery(id+"F0.wireOp",EDGE,"E254");var subQ18=sQuery(id+"F0.wireOp",EDGE,"E253");var subQ19=sQuery(id+"F0.wireOp",EDGE,"E252");var subQ20=sQuery(id+"F0.wireOp",EDGE,"E251");var subQ21=sQuery(id+"F0.wireOp",EDGE,"E250");var subQ22=sQuery(id+"F0.wireOp",EDGE,"E249");var subQ23=sQuery(id+"F0.wireOp",EDGE,"E248");var subQ24=sQuery(id+"F0.wireOp",EDGE,"E247");var subQ25=sQuery(id+"F0.wireOp",EDGE,"E246");var subQ26=sQuery(id+"F0.wireOp",EDGE,"E245");var subQ27=sQuery(id+"F0.wireOp",EDGE,"E244");var subQ28=sQuery(id+"F0.wireOp",EDGE,"E243");var subQ29=sQuery(id+"F0.wireOp",EDGE,"E242");var subQ30=sQuery(id+"F0.wireOp",EDGE,"E127");var subQ31=sQuery(id+"F0.wireOp",EDGE,"E126");var subQ32=sQuery(id+"F0.wireOp",EDGE,"E125");var subQ33=sQuery(id+"F0.wireOp",EDGE,"E124");var subQ34=sQuery(id+"F0.wireOp",EDGE,"E123");var subQ35=sQuery(id+"F0.wireOp",EDGE,"E122");var subQ36=sQuery(id+"F0.wireOp",EDGE,"E121");var subQ37=sQuery(id+"F0.wireOp",EDGE,"E120");var subQ38=sQuery(id+"F0.wireOp",EDGE,"E56");var subQ39=sQuery(id+"F0.wireOp",EDGE,"E55");var subQ40=sQuery(id+"F0.wireOp",EDGE,"E54");var subQ41=sQuery(id+"F0.wireOp",EDGE,"E53");var subQ42=sQuery(id+"F0.wireOp",EDGE,"E52");var subQ43=sQuery(id+"F0.wireOp",EDGE,"E51");var subQ44=sQuery(id+"F0.wireOp",EDGE,"E50");var subQ45=sQuery(id+"F0.wireOp",EDGE,"E49");var subQ46=sQuery(id+"F0.wireOp",EDGE,"E48");var subQ47=sQuery(id+"F0.wireOp",EDGE,"E47");var subQ48=sQuery(id+"F0.wireOp",EDGE,"E46");Q6=makeQuery(id+"F3.opExtrude","SWEPT_BODY",BODY,{"disambiguationData":[OSD([subQ48,subQ47,subQ46,subQ45,subQ44,subQ43,subQ42,subQ41,subQ40,subQ39,subQ38,subQ37,subQ36,subQ35,subQ34,subQ33,subQ32,subQ31,subQ30,subQ29,subQ28,subQ27,subQ26,subQ25,subQ24,subQ23,subQ22,subQ21,subQ20,subQ19,subQ18,subQ17,subQ16,subQ15,subQ14,subQ13,subQ12,subQ11,subQ10,subQ9,subQ8,subQ7,subQ6,subQ5,subQ4,subQ3,subQ2,subQ1,subQ0]),TDD([makeQuery(id+"F2.boolean.opBoolean","SPLIT",FACE,{"disambiguationData":[TD([makeQuery(id+"F2.opExtrude","SWEPT_FACE",FACE,{"disambiguationData":[OSD([sQuery(id+"F0.wireOp",EDGE,"E0")])]})])],"derivedFrom":makeQuery(id+"F1.opExtrude","CAP_FACE",FACE,{"disambiguationData":[OSD([subQ48,subQ47,subQ46,subQ45,subQ44,subQ43,subQ42,subQ41,subQ40,subQ39,subQ38,subQ37,subQ36,subQ35,subQ34,subQ33,subQ32,subQ31,subQ30,subQ29,subQ28,subQ27,subQ26,subQ25,subQ24,subQ23,subQ22,subQ21,subQ20,subQ19,subQ18,subQ17,subQ16,subQ15,subQ14,subQ13,subQ12,subQ11,subQ10,subQ9,subQ8,subQ7,subQ6,subQ5,subQ4,subQ3,subQ2,subQ1,subQ0])],"isStart":false})})])]});}
            var Q7;
            {var subQ0=sQuery(id+"F0.wireOp",EDGE,"E271");var subQ1=sQuery(id+"F0.wireOp",EDGE,"E270");var subQ2=sQuery(id+"F0.wireOp",EDGE,"E269");var subQ3=sQuery(id+"F0.wireOp",EDGE,"E268");var subQ4=sQuery(id+"F0.wireOp",EDGE,"E267");var subQ5=sQuery(id+"F0.wireOp",EDGE,"E266");var subQ6=sQuery(id+"F0.wireOp",EDGE,"E265");var subQ7=sQuery(id+"F0.wireOp",EDGE,"E264");var subQ8=sQuery(id+"F0.wireOp",EDGE,"E263");var subQ9=sQuery(id+"F0.wireOp",EDGE,"E262");var subQ10=sQuery(id+"F0.wireOp",EDGE,"E261");var subQ11=sQuery(id+"F0.wireOp",EDGE,"E260");var subQ12=sQuery(id+"F0.wireOp",EDGE,"E259");var subQ13=sQuery(id+"F0.wireOp",EDGE,"E258");var subQ14=sQuery(id+"F0.wireOp",EDGE,"E257");var subQ15=sQuery(id+"F0.wireOp",EDGE,"E256");var subQ16=sQuery(id+"F0.wireOp",EDGE,"E255");var subQ17=sQuery(id+"F0.wireOp",EDGE,"E254");var subQ18=sQuery(id+"F0.wireOp",EDGE,"E253");var subQ19=sQuery(id+"F0.wireOp",EDGE,"E252");var subQ20=sQuery(id+"F0.wireOp",EDGE,"E251");var subQ21=sQuery(id+"F0.wireOp",EDGE,"E250");var subQ22=sQuery(id+"F0.wireOp",EDGE,"E249");var subQ23=sQuery(id+"F0.wireOp",EDGE,"E248");var subQ24=sQuery(id+"F0.wireOp",EDGE,"E247");var subQ25=sQuery(id+"F0.wireOp",EDGE,"E246");var subQ26=sQuery(id+"F0.wireOp",EDGE,"E245");var subQ27=sQuery(id+"F0.wireOp",EDGE,"E244");var subQ28=sQuery(id+"F0.wireOp",EDGE,"E243");var subQ29=sQuery(id+"F0.wireOp",EDGE,"E242");var subQ30=sQuery(id+"F0.wireOp",EDGE,"E127");var subQ31=sQuery(id+"F0.wireOp",EDGE,"E126");var subQ32=sQuery(id+"F0.wireOp",EDGE,"E125");var subQ33=sQuery(id+"F0.wireOp",EDGE,"E124");var subQ34=sQuery(id+"F0.wireOp",EDGE,"E123");var subQ35=sQuery(id+"F0.wireOp",EDGE,"E122");var subQ36=sQuery(id+"F0.wireOp",EDGE,"E121");var subQ37=sQuery(id+"F0.wireOp",EDGE,"E120");var subQ38=sQuery(id+"F0.wireOp",EDGE,"E56");var subQ39=sQuery(id+"F0.wireOp",EDGE,"E55");var subQ40=sQuery(id+"F0.wireOp",EDGE,"E54");var subQ41=sQuery(id+"F0.wireOp",EDGE,"E53");var subQ42=sQuery(id+"F0.wireOp",EDGE,"E52");var subQ43=sQuery(id+"F0.wireOp",EDGE,"E51");var subQ44=sQuery(id+"F0.wireOp",EDGE,"E50");var subQ45=sQuery(id+"F0.wireOp",EDGE,"E49");var subQ46=sQuery(id+"F0.wireOp",EDGE,"E48");var subQ47=sQuery(id+"F0.wireOp",EDGE,"E47");var subQ48=sQuery(id+"F0.wireOp",EDGE,"E46");Q7=makeQuery(id+"F3.opExtrude","SWEPT_BODY",BODY,{"disambiguationData":[OSD([subQ48,subQ47,subQ46,subQ45,subQ44,subQ43,subQ42,subQ41,subQ40,subQ39,subQ38,subQ37,subQ36,subQ35,subQ34,subQ33,subQ32,subQ31,subQ30,subQ29,subQ28,subQ27,subQ26,subQ25,subQ24,subQ23,subQ22,subQ21,subQ20,subQ19,subQ18,subQ17,subQ16,subQ15,subQ14,subQ13,subQ12,subQ11,subQ10,subQ9,subQ8,subQ7,subQ6,subQ5,subQ4,subQ3,subQ2,subQ1,subQ0]),TDD([makeQuery(id+"F2.boolean.opBoolean","SPLIT",FACE,{"disambiguationData":[TD([makeQuery(id+"F2.opExtrude","SWEPT_FACE",FACE,{"disambiguationData":[OSD([sQuery(id+"F0.wireOp",EDGE,"E140")])]})])],"derivedFrom":makeQuery(id+"F1.opExtrude","CAP_FACE",FACE,{"disambiguationData":[OSD([subQ48,subQ47,subQ46,subQ45,subQ44,subQ43,subQ42,subQ41,subQ40,subQ39,subQ38,subQ37,subQ36,subQ35,subQ34,subQ33,subQ32,subQ31,subQ30,subQ29,subQ28,subQ27,subQ26,subQ25,subQ24,subQ23,subQ22,subQ21,subQ20,subQ19,subQ18,subQ17,subQ16,subQ15,subQ14,subQ13,subQ12,subQ11,subQ10,subQ9,subQ8,subQ7,subQ6,subQ5,subQ4,subQ3,subQ2,subQ1,subQ0])],"isStart":false})})])]});}
            var Q8;
            Q8=sQuery(id+"F5.wireOp",EDGE,"E273");
            transform(context, id + "F6", {"entities" : qUnion([Q0, Q1, Q2, Q3, Q4, Q5, Q6, Q7]), "transformType" : TransformType.ROTATION, "transformAxis" : qUnion([Q8]), "angle" : 90 * degree, "makeCopy" : false});
        }
    });
